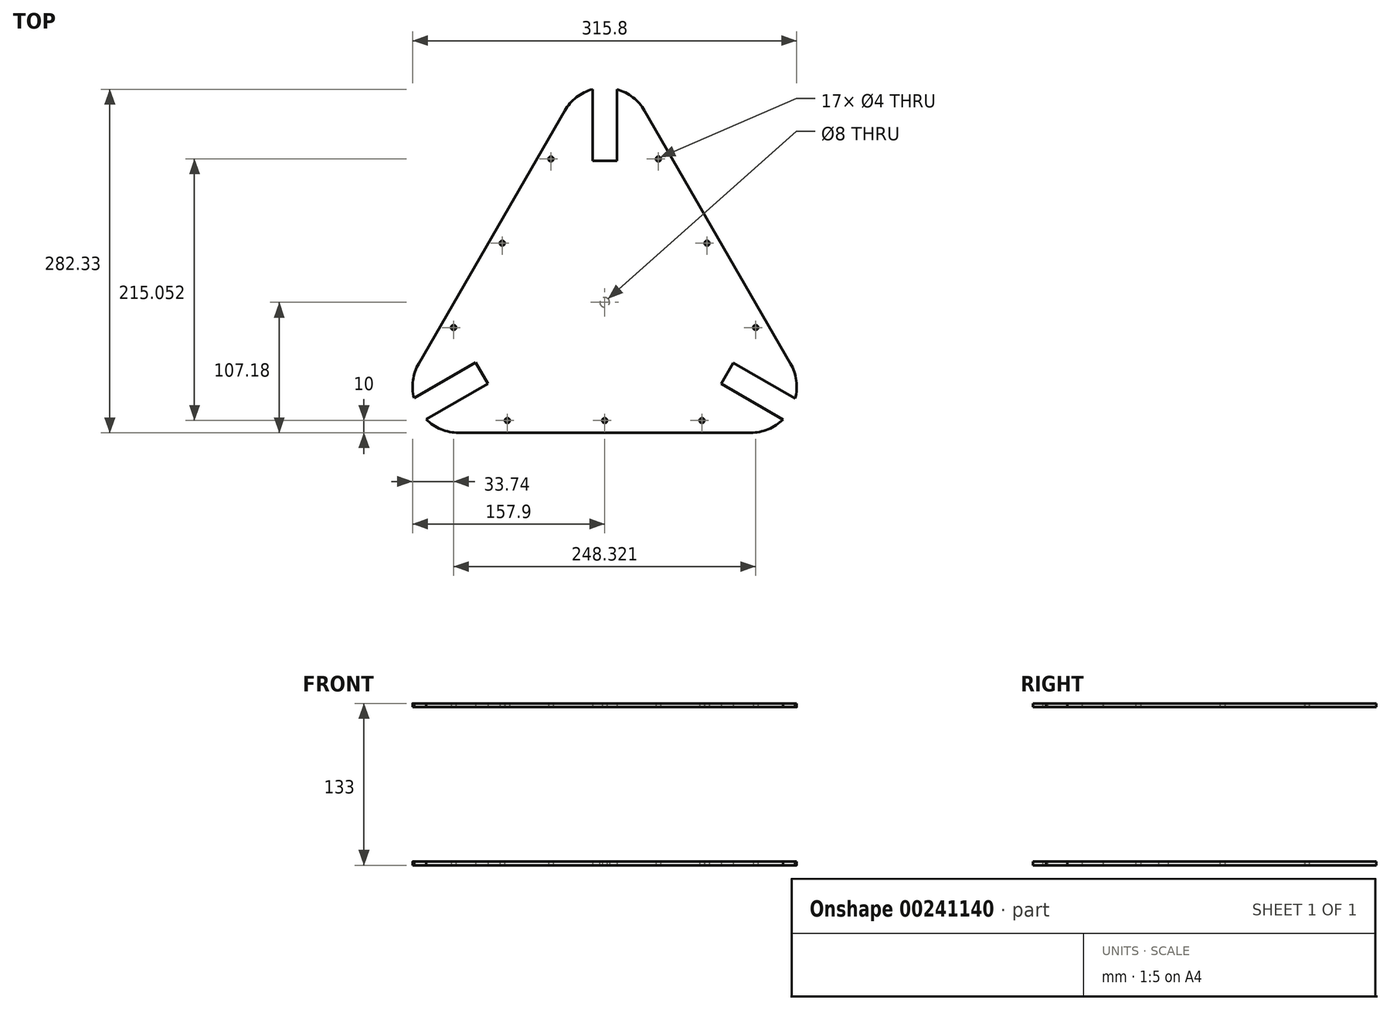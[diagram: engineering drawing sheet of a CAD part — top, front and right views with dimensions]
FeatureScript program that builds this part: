
annotation { "Feature Type Name" : "Feature", "Feature Type Description" : "" }
export const myFeature = defineFeature(function(context is Context, id is Id, definition is map)
    precondition{}
    {
        {
            var Q0;
            Q0=qCreatedBy(makeId("Top.planeOp"),FACE);
            var sketch = newSketch(context, id + "F0", { "sketchPlane" : qUnion([Q0])});
            skLineSegment(sketch, "E0.bottom", {"start": v(-120, -87.18) * mm, "end": v(120, -87.18) * mm});
            skLineSegment(sketch, "E0.top", {"start": v(-120, -107.18) * mm, "end": v(120, -107.18) * mm});
            skLineSegment(sketch, "E0.left", {"start": v(-120, -87.18) * mm, "end": v(-120, -107.18) * mm});
            skLineSegment(sketch, "E0.right", {"start": v(120, -87.18) * mm, "end": v(120, -107.18) * mm});
            skLineSegment(sketch, "E1.1.0", {"start": v(135.5, -60.33) * mm, "end": v(152.82, -50.33) * mm});
            skLineSegment(sketch, "E1.1.1", {"start": v(135.5, -60.33) * mm, "end": v(15.5, 147.51) * mm});
            skLineSegment(sketch, "E1.1.2", {"start": v(152.82, -50.33) * mm, "end": v(32.82, 157.51) * mm});
            skLineSegment(sketch, "E1.1.3", {"start": v(15.5, 147.51) * mm, "end": v(32.82, 157.51) * mm});
            skLineSegment(sketch, "E1.2.0", {"start": v(-15.5, 147.51) * mm, "end": v(-32.82, 157.51) * mm});
            skLineSegment(sketch, "E1.2.1", {"start": v(-15.5, 147.51) * mm, "end": v(-135.5, -60.33) * mm});
            skLineSegment(sketch, "E1.2.2", {"start": v(-32.82, 157.51) * mm, "end": v(-152.82, -50.33) * mm});
            skLineSegment(sketch, "E1.2.3", {"start": v(-135.5, -60.33) * mm, "end": v(-152.82, -50.33) * mm});
            skPoint(sketch, "E1.center", {"position": v(0, 0) * mm});
            skArc(sketch, "E2", {"start": v(-152.82, -50.33) * mm, "mid": v(-152.82, -88.23) * mm, "end": v(-120, -107.18) * mm});
            skArc(sketch, "E3", {"start": v(120, -107.18) * mm, "mid": v(152.82, -88.23) * mm, "end": v(152.82, -50.33) * mm});
            skArc(sketch, "E4", {"start": v(32.82, 157.51) * mm, "mid": v(0, 176.46) * mm, "end": v(-32.82, 157.51) * mm});
            skPoint(sketch, "E5.orphan", {"position": v(-92.82, 53.59) * mm});
            skPoint(sketch, "E6.middle.positionSnap0", {"position": v(0, 176.46) * mm});
            skPoint(sketch, "E6.centerSnap0", {"position": v(0, 176.46) * mm});
            skLineSegment(sketch, "E7", {"start": v(-144.16, -55.33) * mm, "end": v(-129.16, -29.35) * mm, "construction": true});
            skLineSegment(sketch, "E8", {"start": v(-120, -107.18) * mm, "end": v(-120, -113.18) * mm, "construction": true});
            skLineSegment(sketch, "E9", {"start": v(-110, -113.18) * mm, "end": v(-110, -116.18) * mm});
            skLineSegment(sketch, "E10", {"start": v(-159.07, -116.18) * mm, "end": v(-159.07, -116.18) * mm});
            skPoint(sketch, "E11.visualSharp", {"position": v(-172.46, -135.5) * mm});
            skPoint(sketch, "E12.visualSharp", {"position": v(-159.07, -118.18) * mm});
            skArc(sketch, "E13", {"start": v(-120, -87.18) * mm, "mid": v(-104.5, -60.33) * mm, "end": v(-135.5, -60.33) * mm, "construction": true});
            skLineSegment(sketch, "E14", {"start": v(-92.82, 53.59) * mm, "end": v(-75.5, 43.59) * mm, "construction": true});
            skLineSegment(sketch, "E15", {"start": v(-115.56, 26.2) * mm, "end": v(-118.16, 27.7) * mm});
            skLineSegment(sketch, "E16", {"start": v(-77.66, 91.84) * mm, "end": v(-80.26, 93.34) * mm});
            skLineSegment(sketch, "E17.anchor1", {"start": v(0, 0) * mm, "end": v(158.2, -91.34) * mm, "construction": true});
            skLineSegment(sketch, "E17.anchor2", {"start": v(0, 0) * mm, "end": v(0, 180.31) * mm, "construction": true});
            skLineSegment(sketch, "E18", {"start": v(-75.5, 43.59) * mm, "end": v(-72.38, 41.79) * mm, "construction": true});
            skCircle(sketch, "E19", {"center": v(-80, -97.18) * mm, "radius": 2 * mm});
            skLineSegment(sketch, "E20.direction1", {"start": v(-80, -97.18) * mm, "end": v(-78.5, -97.18) * mm, "construction": true});
            skLineSegment(sketch, "E21.direction1", {"start": v(-80, -97.18) * mm, "end": v(-81.5, -97.18) * mm, "construction": true});
            skLineSegment(sketch, "E22", {"start": v(0, -87.18) * mm, "end": v(0, -107.18) * mm, "construction": true});
            skLineSegment(sketch, "E23", {"start": v(-120, -87.18) * mm, "end": v(-135.5, -60.33) * mm, "construction": true});
            skCircle(sketch, "E24", {"center": v(-127.75, -73.76) * mm, "radius": 4 * mm});
            skLineSegment(sketch, "E25", {"start": v(-129.8, -50.45) * mm, "end": v(-108.59, -87.18) * mm, "construction": true});
            skLineSegment(sketch, "E26.MirrorCS", {"start": v(80, -97.18) * mm, "end": v(78.5, -97.18) * mm, "construction": true});
            skLineSegment(sketch, "E27.MirrorCS", {"start": v(80, -97.18) * mm, "end": v(81.5, -97.18) * mm, "construction": true});
            skCircle(sketch, "E28.MirrorC", {"center": v(80, -97.18) * mm, "radius": 2 * mm});
            skCircle(sketch, "E29.1.2", {"center": v(127.8, -73.86) * mm, "radius": 4 * mm});
            skCircle(sketch, "E29.2.2", {"center": v(0.12, 147.51) * mm, "radius": 4 * mm});
            skPoint(sketch, "E29.center", {"position": v(0.06, -0.03) * mm});
            skCircle(sketch, "E30", {"center": v(0, 0) * mm, "radius": 4 * mm});
            skLineSegment(sketch, "E31", {"start": v(0, 116.46) * mm, "end": v(-29.5, 116.46) * mm, "construction": true});
            skLineSegment(sketch, "E32.bottom", {"start": v(-9.88, 185.6) * mm, "end": v(10.12, 185.6) * mm});
            skLineSegment(sketch, "E32.left", {"start": v(-9.88, 185.6) * mm, "end": v(-9.88, 109.43) * mm});
            skLineSegment(sketch, "E32.right", {"start": v(10.12, 185.6) * mm, "end": v(10.12, 109.43) * mm});
            skLineSegment(sketch, "E33", {"start": v(-9.88, 116.46) * mm, "end": v(10.12, 116.46) * mm});
            skArc(sketch, "E34", {"start": v(-9.88, 104.53) * mm, "mid": v(0.12, 102.8) * mm, "end": v(10.12, 104.51) * mm});
            skLineSegment(sketch, "E35.1.0", {"start": v(-155.79, -101.35) * mm, "end": v(-89.83, -63.27) * mm});
            skLineSegment(sketch, "E35.1.1", {"start": v(-95.92, -66.79) * mm, "end": v(-105.92, -49.47) * mm});
            skLineSegment(sketch, "E35.1.2", {"start": v(-165.79, -84.03) * mm, "end": v(-99.83, -45.95) * mm});
            skLineSegment(sketch, "E35.2.0", {"start": v(165.67, -84.24) * mm, "end": v(99.71, -46.16) * mm});
            skLineSegment(sketch, "E35.2.1", {"start": v(105.8, -49.67) * mm, "end": v(95.8, -67) * mm});
            skLineSegment(sketch, "E35.2.2", {"start": v(155.67, -101.56) * mm, "end": v(89.71, -63.48) * mm});
            skCircle(sketch, "E36.1.0", {"center": v(124.16, -20.7) * mm, "radius": 2 * mm});
            skCircle(sketch, "E36.1.1", {"center": v(44.16, 117.87) * mm, "radius": 2 * mm});
            skCircle(sketch, "E36.2.0", {"center": v(-44.16, 117.87) * mm, "radius": 2 * mm});
            skCircle(sketch, "E36.2.1", {"center": v(-124.16, -20.7) * mm, "radius": 2 * mm});
            skCircle(sketch, "E37", {"center": v(0, -97.18) * mm, "radius": 2 * mm});
            skCircle(sketch, "E38.1.0", {"center": v(84.16, 48.59) * mm, "radius": 2 * mm});
            skCircle(sketch, "E38.2.0", {"center": v(-84.16, 48.59) * mm, "radius": 2 * mm});
            skSolve(sketch);
        }
        {
            var Q0;
            {var subQ0=sQuery(id+"F0.wireOp",EDGE,"E21.1.0.0");var subQ1=sQuery(id+"F0.wireOp",EDGE,"E20.2.0.0");var subQ2=makeQuery(id+"F0.imprint","INTERSECT",VERTEX,{"disambiguationData":[OD(0.0)],"derivedFrom":[subQ1,subQ0]});Q0=makeQuery(id+"F0.imprint","IMPRINT",FACE,{"disambiguationData":[TD([[makeQuery(id+"F0.imprint","IMPRINT",EDGE,{"disambiguationData":[TD([[subQ2,-1.0]])],"derivedFrom":subQ1}),1.0]])]});}
            var Q1;
            {var subQ0=sQuery(id+"F0.wireOp",EDGE,"E20.2.0.0");var subQ1=sQuery(id+"F0.wireOp",EDGE,"E20.1.0.0");var subQ2=makeQuery(id+"F0.imprint","INTERSECT",VERTEX,{"disambiguationData":[OD(0.0)],"derivedFrom":[subQ1,subQ0]});Q1=makeQuery(id+"F0.imprint","IMPRINT",FACE,{"disambiguationData":[TD([[makeQuery(id+"F0.imprint","IMPRINT",EDGE,{"disambiguationData":[TD([[subQ2,1.0]])],"derivedFrom":subQ1}),-1.0]])]});}
            var Q2;
            {var subQ0=sQuery(id+"F0.wireOp",EDGE,"E21.2.0.0");var subQ1=sQuery(id+"F0.wireOp",EDGE,"E21.1.0.0");var subQ2=makeQuery(id+"F0.imprint","INTERSECT",VERTEX,{"disambiguationData":[OD(0.0)],"derivedFrom":[subQ1,subQ0]});Q2=makeQuery(id+"F0.imprint","IMPRINT",FACE,{"disambiguationData":[TD([[makeQuery(id+"F0.imprint","IMPRINT",EDGE,{"disambiguationData":[TD([[subQ2,-1.0]])],"derivedFrom":subQ1}),-1.0]])]});}
            var Q3;
            {var subQ0=sQuery(id+"F0.wireOp",EDGE,"E21.2.0.0");var subQ1=sQuery(id+"F0.wireOp",EDGE,"E20.1.0.0");var subQ2=makeQuery(id+"F0.imprint","INTERSECT",VERTEX,{"disambiguationData":[OD(1.0)],"derivedFrom":[subQ1,subQ0]});Q3=makeQuery(id+"F0.imprint","IMPRINT",FACE,{"disambiguationData":[TD([[makeQuery(id+"F0.imprint","IMPRINT",EDGE,{"disambiguationData":[TD([[subQ2,-1.0]])],"derivedFrom":subQ1}),1.0]])]});}
            var Q4;
            {var subQ0=sQuery(id+"F0.wireOp",EDGE,"E20.2.0.0");var subQ1=sQuery(id+"F0.wireOp",EDGE,"E19");var subQ2=makeQuery(id+"F0.imprint","INTERSECT",VERTEX,{"disambiguationData":[OD(0.0)],"derivedFrom":[subQ1,subQ0]});Q4=makeQuery(id+"F0.imprint","IMPRINT",FACE,{"disambiguationData":[TD([[makeQuery(id+"F0.imprint","IMPRINT",EDGE,{"disambiguationData":[TD([[subQ2,1.0]])],"derivedFrom":subQ1}),1.0]])]});}
            var Q5;
            {var subQ0=sQuery(id+"F0.wireOp",EDGE,"E21.1.0.0");var subQ1=sQuery(id+"F0.wireOp",EDGE,"E20.1.0.0");var subQ2=makeQuery(id+"F0.imprint","INTERSECT",VERTEX,{"disambiguationData":[OD(0.0)],"derivedFrom":[subQ1,subQ0]});Q5=makeQuery(id+"F0.imprint","IMPRINT",FACE,{"disambiguationData":[TD([[makeQuery(id+"F0.imprint","IMPRINT",EDGE,{"disambiguationData":[TD([[subQ2,-1.0]])],"derivedFrom":subQ1}),1.0]])]});}
            var Q6;
            {var subQ0=sQuery(id+"F0.wireOp",EDGE,"E21.2.0.0");var subQ1=sQuery(id+"F0.wireOp",EDGE,"E19");var subQ2=makeQuery(id+"F0.imprint","INTERSECT",VERTEX,{"disambiguationData":[OD(0.0)],"derivedFrom":[subQ1,subQ0]});Q6=makeQuery(id+"F0.imprint","IMPRINT",FACE,{"disambiguationData":[TD([[makeQuery(id+"F0.imprint","IMPRINT",EDGE,{"disambiguationData":[TD([[subQ2,-1.0]])],"derivedFrom":subQ1}),1.0]])]});}
            var Q7;
            {var subQ0=sQuery(id+"F0.wireOp",EDGE,"E21.2.0.0");var subQ1=sQuery(id+"F0.wireOp",EDGE,"E19");var subQ2=makeQuery(id+"F0.imprint","INTERSECT",VERTEX,{"disambiguationData":[OD(0.0)],"derivedFrom":[subQ1,subQ0]});Q7=makeQuery(id+"F0.imprint","IMPRINT",FACE,{"disambiguationData":[TD([[makeQuery(id+"F0.imprint","IMPRINT",EDGE,{"disambiguationData":[TD([[subQ2,-1.0]])],"derivedFrom":subQ1}),-1.0]])]});}
            var Q8;
            {var subQ0=sQuery(id+"F0.wireOp",EDGE,"E20.2.0.0");var subQ1=sQuery(id+"F0.wireOp",EDGE,"E19");var subQ2=makeQuery(id+"F0.imprint","INTERSECT",VERTEX,{"disambiguationData":[OD(0.0)],"derivedFrom":[subQ1,subQ0]});Q8=makeQuery(id+"F0.imprint","IMPRINT",FACE,{"disambiguationData":[TD([[makeQuery(id+"F0.imprint","IMPRINT",EDGE,{"disambiguationData":[TD([[subQ2,1.0]])],"derivedFrom":subQ1}),-1.0]])]});}
            var Q9;
            {var subQ0=sQuery(id+"F0.wireOp",EDGE,"E20.1.0.0");var subQ1=sQuery(id+"F0.wireOp",EDGE,"E19");var subQ2=makeQuery(id+"F0.imprint","INTERSECT",VERTEX,{"disambiguationData":[OD(0.0)],"derivedFrom":[subQ1,subQ0]});Q9=makeQuery(id+"F0.imprint","IMPRINT",FACE,{"disambiguationData":[TD([[makeQuery(id+"F0.imprint","IMPRINT",EDGE,{"disambiguationData":[TD([[subQ2,1.0]])],"derivedFrom":subQ1}),1.0]])]});}
            var Q10;
            {var subQ0=sQuery(id+"F0.wireOp",EDGE,"E20.1.0.0");var subQ1=sQuery(id+"F0.wireOp",EDGE,"E19");var subQ2=makeQuery(id+"F0.imprint","INTERSECT",VERTEX,{"disambiguationData":[OD(0.0)],"derivedFrom":[subQ1,subQ0]});Q10=makeQuery(id+"F0.imprint","IMPRINT",FACE,{"disambiguationData":[TD([[makeQuery(id+"F0.imprint","IMPRINT",EDGE,{"disambiguationData":[TD([[subQ2,-1.0]])],"derivedFrom":subQ1}),1.0]])]});}
            var Q11;
            {var subQ0=sQuery(id+"F0.wireOp",EDGE,"E21.1.0.0");var subQ1=sQuery(id+"F0.wireOp",EDGE,"E19");var subQ2=makeQuery(id+"F0.imprint","INTERSECT",VERTEX,{"disambiguationData":[OD(0.0)],"derivedFrom":[subQ1,subQ0]});Q11=makeQuery(id+"F0.imprint","IMPRINT",FACE,{"disambiguationData":[TD([[makeQuery(id+"F0.imprint","IMPRINT",EDGE,{"disambiguationData":[TD([[subQ2,-1.0]])],"derivedFrom":subQ1}),-1.0]])]});}
            var Q12;
            {var subQ0=sQuery(id+"F0.wireOp",EDGE,"E21.2.0.0");var subQ1=sQuery(id+"F0.wireOp",EDGE,"E20.1.0.0");var subQ2=makeQuery(id+"F0.imprint","INTERSECT",VERTEX,{"disambiguationData":[OD(0.0)],"derivedFrom":[subQ1,subQ0]});Q12=makeQuery(id+"F0.imprint","IMPRINT",FACE,{"disambiguationData":[TD([[makeQuery(id+"F0.imprint","IMPRINT",EDGE,{"disambiguationData":[TD([[subQ2,-1.0]])],"derivedFrom":subQ1}),1.0]])]});}
            var Q13;
            {var subQ0=sQuery(id+"F0.wireOp",EDGE,"E21.1.0.0");var subQ1=sQuery(id+"F0.wireOp",EDGE,"E19");var subQ2=makeQuery(id+"F0.imprint","INTERSECT",VERTEX,{"disambiguationData":[OD(1.0)],"derivedFrom":[subQ1,subQ0]});Q13=makeQuery(id+"F0.imprint","IMPRINT",FACE,{"disambiguationData":[TD([[makeQuery(id+"F0.imprint","IMPRINT",EDGE,{"disambiguationData":[TD([[subQ2,-1.0]])],"derivedFrom":subQ1}),1.0]])]});}
            var Q14;
            {var subQ0=sQuery(id+"F0.wireOp",EDGE,"E20.1.0.0");var subQ1=sQuery(id+"F0.wireOp",EDGE,"E19");var subQ2=makeQuery(id+"F0.imprint","INTERSECT",VERTEX,{"disambiguationData":[OD(1.0)],"derivedFrom":[subQ1,subQ0]});Q14=makeQuery(id+"F0.imprint","IMPRINT",FACE,{"disambiguationData":[TD([[makeQuery(id+"F0.imprint","IMPRINT",EDGE,{"disambiguationData":[TD([[subQ2,-1.0]])],"derivedFrom":subQ1}),-1.0]])]});}
            var Q15;
            {var subQ0=sQuery(id+"F0.wireOp",EDGE,"E20.1.0.0");var subQ1=sQuery(id+"F0.wireOp",EDGE,"E19");var subQ2=makeQuery(id+"F0.imprint","INTERSECT",VERTEX,{"disambiguationData":[OD(0.0)],"derivedFrom":[subQ1,subQ0]});Q15=makeQuery(id+"F0.imprint","IMPRINT",FACE,{"disambiguationData":[TD([[makeQuery(id+"F0.imprint","IMPRINT",EDGE,{"disambiguationData":[TD([[subQ2,1.0]])],"derivedFrom":subQ1}),-1.0]])]});}
            var Q16;
            {var subQ0=sQuery(id+"F0.wireOp",EDGE,"E21.1.0.0");var subQ1=sQuery(id+"F0.wireOp",EDGE,"E19");var subQ2=makeQuery(id+"F0.imprint","INTERSECT",VERTEX,{"disambiguationData":[OD(0.0)],"derivedFrom":[subQ1,subQ0]});Q16=makeQuery(id+"F0.imprint","IMPRINT",FACE,{"disambiguationData":[TD([[makeQuery(id+"F0.imprint","IMPRINT",EDGE,{"disambiguationData":[TD([[subQ2,-1.0]])],"derivedFrom":subQ1}),1.0]])]});}
            var Q17;
            {var subQ0=sQuery(id+"F0.wireOp",EDGE,"E21.2.0.0");var subQ1=sQuery(id+"F0.wireOp",EDGE,"E19");var subQ2=makeQuery(id+"F0.imprint","INTERSECT",VERTEX,{"disambiguationData":[OD(1.0)],"derivedFrom":[subQ1,subQ0]});Q17=makeQuery(id+"F0.imprint","IMPRINT",FACE,{"disambiguationData":[TD([[makeQuery(id+"F0.imprint","IMPRINT",EDGE,{"disambiguationData":[TD([[subQ2,-1.0]])],"derivedFrom":subQ1}),1.0]])]});}
            var Q18;
            {var subQ0=sQuery(id+"F0.wireOp",EDGE,"E21.2.0.0");var subQ1=sQuery(id+"F0.wireOp",EDGE,"E19");var subQ2=makeQuery(id+"F0.imprint","INTERSECT",VERTEX,{"disambiguationData":[OD(1.0)],"derivedFrom":[subQ1,subQ0]});Q18=makeQuery(id+"F0.imprint","IMPRINT",FACE,{"disambiguationData":[TD([[makeQuery(id+"F0.imprint","IMPRINT",EDGE,{"disambiguationData":[TD([[subQ2,-1.0]])],"derivedFrom":subQ1}),-1.0]])]});}
            var Q19;
            {var subQ0=sQuery(id+"F0.wireOp",EDGE,"E20.1.0.0");var subQ1=sQuery(id+"F0.wireOp",EDGE,"E19");var subQ2=makeQuery(id+"F0.imprint","INTERSECT",VERTEX,{"disambiguationData":[OD(1.0)],"derivedFrom":[subQ1,subQ0]});Q19=makeQuery(id+"F0.imprint","IMPRINT",FACE,{"disambiguationData":[TD([[makeQuery(id+"F0.imprint","IMPRINT",EDGE,{"disambiguationData":[TD([[subQ2,-1.0]])],"derivedFrom":subQ1}),1.0]])]});}
            var Q20;
            {var subQ0=sQuery(id+"F0.wireOp",EDGE,"df970ebe-b7b2-4de3-9d96-1b594ea6aba34.MirrorC");var subQ1=sQuery(id+"F0.wireOp",EDGE,"df970ebe-b7b2-4de3-9d96-1b594ea6aba33.MirrorC");var subQ2=makeQuery(id+"F0.imprint","INTERSECT",VERTEX,{"disambiguationData":[OD(0.0)],"derivedFrom":[subQ1,subQ0]});Q20=makeQuery(id+"F0.imprint","IMPRINT",FACE,{"disambiguationData":[TD([[makeQuery(id+"F0.imprint","IMPRINT",EDGE,{"disambiguationData":[TD([[subQ2,-1.0]])],"derivedFrom":subQ1}),-1.0]])]});}
            var Q21;
            {var subQ0=sQuery(id+"F0.wireOp",EDGE,"df970ebe-b7b2-4de3-9d96-1b594ea6aba36.MirrorC");var subQ1=sQuery(id+"F0.wireOp",EDGE,"df970ebe-b7b2-4de3-9d96-1b594ea6aba32.MirrorC");var subQ2=makeQuery(id+"F0.imprint","INTERSECT",VERTEX,{"disambiguationData":[OD(0.0)],"derivedFrom":[subQ1,subQ0]});Q21=makeQuery(id+"F0.imprint","IMPRINT",FACE,{"disambiguationData":[TD([[makeQuery(id+"F0.imprint","IMPRINT",EDGE,{"disambiguationData":[TD([[subQ2,-1.0]])],"derivedFrom":subQ1}),1.0]])]});}
            var Q22;
            {var subQ0=sQuery(id+"F0.wireOp",EDGE,"E28.MirrorC");var subQ1=sQuery(id+"F0.wireOp",EDGE,"df970ebe-b7b2-4de3-9d96-1b594ea6aba32.MirrorC");var subQ2=makeQuery(id+"F0.imprint","INTERSECT",VERTEX,{"disambiguationData":[OD(0.0)],"derivedFrom":[subQ1,subQ0]});Q22=makeQuery(id+"F0.imprint","IMPRINT",FACE,{"disambiguationData":[TD([[makeQuery(id+"F0.imprint","IMPRINT",EDGE,{"disambiguationData":[TD([[subQ2,1.0]])],"derivedFrom":subQ1}),-1.0]])]});}
            var Q23;
            {var subQ0=sQuery(id+"F0.wireOp",EDGE,"E28.MirrorC");var subQ1=sQuery(id+"F0.wireOp",EDGE,"df970ebe-b7b2-4de3-9d96-1b594ea6aba33.MirrorC");var subQ2=makeQuery(id+"F0.imprint","INTERSECT",VERTEX,{"disambiguationData":[OD(0.0)],"derivedFrom":[subQ1,subQ0]});Q23=makeQuery(id+"F0.imprint","IMPRINT",FACE,{"disambiguationData":[TD([[makeQuery(id+"F0.imprint","IMPRINT",EDGE,{"disambiguationData":[TD([[subQ2,-1.0]])],"derivedFrom":subQ1}),-1.0]])]});}
            var Q24;
            {var subQ0=sQuery(id+"F0.wireOp",EDGE,"df970ebe-b7b2-4de3-9d96-1b594ea6aba36.MirrorC");var subQ1=sQuery(id+"F0.wireOp",EDGE,"df970ebe-b7b2-4de3-9d96-1b594ea6aba32.MirrorC");var subQ2=makeQuery(id+"F0.imprint","INTERSECT",VERTEX,{"disambiguationData":[OD(0.0)],"derivedFrom":[subQ1,subQ0]});Q24=makeQuery(id+"F0.imprint","IMPRINT",FACE,{"disambiguationData":[TD([[makeQuery(id+"F0.imprint","IMPRINT",EDGE,{"disambiguationData":[TD([[subQ2,-1.0]])],"derivedFrom":subQ1}),-1.0]])]});}
            var Q25;
            {var subQ0=sQuery(id+"F0.wireOp",EDGE,"E28.MirrorC");var subQ1=sQuery(id+"F0.wireOp",EDGE,"df970ebe-b7b2-4de3-9d96-1b594ea6aba32.MirrorC");var subQ2=makeQuery(id+"F0.imprint","INTERSECT",VERTEX,{"disambiguationData":[OD(0.0)],"derivedFrom":[subQ1,subQ0]});Q25=makeQuery(id+"F0.imprint","IMPRINT",FACE,{"disambiguationData":[TD([[makeQuery(id+"F0.imprint","IMPRINT",EDGE,{"disambiguationData":[TD([[subQ2,-1.0]])],"derivedFrom":subQ1}),-1.0]])]});}
            var Q26;
            {var subQ0=sQuery(id+"F0.wireOp",EDGE,"df970ebe-b7b2-4de3-9d96-1b594ea6aba34.MirrorC");var subQ1=sQuery(id+"F0.wireOp",EDGE,"df970ebe-b7b2-4de3-9d96-1b594ea6aba32.MirrorC");var subQ2=makeQuery(id+"F0.imprint","INTERSECT",VERTEX,{"disambiguationData":[OD(0.0)],"derivedFrom":[subQ1,subQ0]});Q26=makeQuery(id+"F0.imprint","IMPRINT",FACE,{"disambiguationData":[TD([[makeQuery(id+"F0.imprint","IMPRINT",EDGE,{"disambiguationData":[TD([[subQ2,1.0]])],"derivedFrom":subQ1}),-1.0]])]});}
            var Q27;
            {var subQ0=sQuery(id+"F0.wireOp",EDGE,"df970ebe-b7b2-4de3-9d96-1b594ea6aba36.MirrorC");var subQ1=sQuery(id+"F0.wireOp",EDGE,"df970ebe-b7b2-4de3-9d96-1b594ea6aba33.MirrorC");var subQ2=makeQuery(id+"F0.imprint","INTERSECT",VERTEX,{"disambiguationData":[OD(0.0)],"derivedFrom":[subQ1,subQ0]});Q27=makeQuery(id+"F0.imprint","IMPRINT",FACE,{"disambiguationData":[TD([[makeQuery(id+"F0.imprint","IMPRINT",EDGE,{"disambiguationData":[TD([[subQ2,-1.0]])],"derivedFrom":subQ1}),-1.0]])]});}
            var Q28;
            {var subQ0=sQuery(id+"F0.wireOp",EDGE,"df970ebe-b7b2-4de3-9d96-1b594ea6aba36.MirrorC");var subQ1=sQuery(id+"F0.wireOp",EDGE,"df970ebe-b7b2-4de3-9d96-1b594ea6aba32.MirrorC");var subQ2=makeQuery(id+"F0.imprint","INTERSECT",VERTEX,{"disambiguationData":[OD(1.0)],"derivedFrom":[subQ1,subQ0]});Q28=makeQuery(id+"F0.imprint","IMPRINT",FACE,{"disambiguationData":[TD([[makeQuery(id+"F0.imprint","IMPRINT",EDGE,{"disambiguationData":[TD([[subQ2,-1.0]])],"derivedFrom":subQ1}),1.0]])]});}
            var Q29;
            {var subQ0=sQuery(id+"F0.wireOp",EDGE,"E28.MirrorC");var subQ1=sQuery(id+"F0.wireOp",EDGE,"df970ebe-b7b2-4de3-9d96-1b594ea6aba32.MirrorC");var subQ2=makeQuery(id+"F0.imprint","INTERSECT",VERTEX,{"disambiguationData":[OD(1.0)],"derivedFrom":[subQ1,subQ0]});Q29=makeQuery(id+"F0.imprint","IMPRINT",FACE,{"disambiguationData":[TD([[makeQuery(id+"F0.imprint","IMPRINT",EDGE,{"disambiguationData":[TD([[subQ2,-1.0]])],"derivedFrom":subQ1}),1.0]])]});}
            var Q30;
            {var subQ0=sQuery(id+"F0.wireOp",EDGE,"E28.MirrorC");var subQ1=sQuery(id+"F0.wireOp",EDGE,"df970ebe-b7b2-4de3-9d96-1b594ea6aba32.MirrorC");var subQ2=makeQuery(id+"F0.imprint","INTERSECT",VERTEX,{"disambiguationData":[OD(0.0)],"derivedFrom":[subQ1,subQ0]});Q30=makeQuery(id+"F0.imprint","IMPRINT",FACE,{"disambiguationData":[TD([[makeQuery(id+"F0.imprint","IMPRINT",EDGE,{"disambiguationData":[TD([[subQ2,1.0]])],"derivedFrom":subQ1}),1.0]])]});}
            var Q31;
            {var subQ0=sQuery(id+"F0.wireOp",EDGE,"df970ebe-b7b2-4de3-9d96-1b594ea6aba33.MirrorC");var subQ1=sQuery(id+"F0.wireOp",EDGE,"df970ebe-b7b2-4de3-9d96-1b594ea6aba32.MirrorC");var subQ2=makeQuery(id+"F0.imprint","INTERSECT",VERTEX,{"derivedFrom":[subQ1,subQ0]});Q31=makeQuery(id+"F0.imprint","IMPRINT",FACE,{"disambiguationData":[TD([[makeQuery(id+"F0.imprint","IMPRINT",EDGE,{"disambiguationData":[TD([[subQ2,-1.0]])],"derivedFrom":subQ1}),1.0]])]});}
            var Q32;
            {var subQ0=sQuery(id+"F0.wireOp",EDGE,"E28.MirrorC");var subQ1=sQuery(id+"F0.wireOp",EDGE,"df970ebe-b7b2-4de3-9d96-1b594ea6aba33.MirrorC");var subQ2=makeQuery(id+"F0.imprint","INTERSECT",VERTEX,{"disambiguationData":[OD(0.0)],"derivedFrom":[subQ1,subQ0]});Q32=makeQuery(id+"F0.imprint","IMPRINT",FACE,{"disambiguationData":[TD([[makeQuery(id+"F0.imprint","IMPRINT",EDGE,{"disambiguationData":[TD([[subQ2,-1.0]])],"derivedFrom":subQ1}),1.0]])]});}
            var Q33;
            {var subQ0=sQuery(id+"F0.wireOp",EDGE,"df970ebe-b7b2-4de3-9d96-1b594ea6aba33.MirrorC");var subQ1=makeQuery(id+"F0.imprint","INTERSECT",VERTEX,{"derivedFrom":[sQuery(id+"F0.wireOp",EDGE,"df970ebe-b7b2-4de3-9d96-1b594ea6aba32.MirrorC"),subQ0]});Q33=makeQuery(id+"F0.imprint","IMPRINT",FACE,{"disambiguationData":[TD([[makeQuery(id+"F0.imprint","IMPRINT",EDGE,{"disambiguationData":[TD([[subQ1,-1.0]])],"derivedFrom":subQ0}),-1.0]])]});}
            var Q34;
            {var subQ0=sQuery(id+"F0.wireOp",EDGE,"df970ebe-b7b2-4de3-9d96-1b594ea6aba34.MirrorC");var subQ1=sQuery(id+"F0.wireOp",EDGE,"df970ebe-b7b2-4de3-9d96-1b594ea6aba33.MirrorC");var subQ2=makeQuery(id+"F0.imprint","INTERSECT",VERTEX,{"disambiguationData":[OD(0.0)],"derivedFrom":[subQ1,subQ0]});Q34=makeQuery(id+"F0.imprint","IMPRINT",FACE,{"disambiguationData":[TD([[makeQuery(id+"F0.imprint","IMPRINT",EDGE,{"disambiguationData":[TD([[subQ2,-1.0]])],"derivedFrom":subQ1}),1.0]])]});}
            var Q35;
            {var subQ0=sQuery(id+"F0.wireOp",EDGE,"df970ebe-b7b2-4de3-9d96-1b594ea6aba36.MirrorC");var subQ1=sQuery(id+"F0.wireOp",EDGE,"df970ebe-b7b2-4de3-9d96-1b594ea6aba34.MirrorC");var subQ2=makeQuery(id+"F0.imprint","INTERSECT",VERTEX,{"disambiguationData":[OD(1.0)],"derivedFrom":[subQ1,subQ0]});Q35=makeQuery(id+"F0.imprint","IMPRINT",FACE,{"disambiguationData":[TD([[makeQuery(id+"F0.imprint","IMPRINT",EDGE,{"disambiguationData":[TD([[subQ2,-1.0]])],"derivedFrom":subQ1}),1.0]])]});}
            var Q36;
            {var subQ0=sQuery(id+"F0.wireOp",EDGE,"E28.MirrorC");var subQ1=sQuery(id+"F0.wireOp",EDGE,"df970ebe-b7b2-4de3-9d96-1b594ea6aba32.MirrorC");var subQ2=makeQuery(id+"F0.imprint","INTERSECT",VERTEX,{"disambiguationData":[OD(0.0)],"derivedFrom":[subQ1,subQ0]});Q36=makeQuery(id+"F0.imprint","IMPRINT",FACE,{"disambiguationData":[TD([[makeQuery(id+"F0.imprint","IMPRINT",EDGE,{"disambiguationData":[TD([[subQ2,-1.0]])],"derivedFrom":subQ1}),1.0]])]});}
            var Q37;
            {var subQ0=sQuery(id+"F0.wireOp",EDGE,"E28.MirrorC");var subQ1=sQuery(id+"F0.wireOp",EDGE,"df970ebe-b7b2-4de3-9d96-1b594ea6aba33.MirrorC");var subQ2=makeQuery(id+"F0.imprint","INTERSECT",VERTEX,{"disambiguationData":[OD(1.0)],"derivedFrom":[subQ1,subQ0]});Q37=makeQuery(id+"F0.imprint","IMPRINT",FACE,{"disambiguationData":[TD([[makeQuery(id+"F0.imprint","IMPRINT",EDGE,{"disambiguationData":[TD([[subQ2,-1.0]])],"derivedFrom":subQ1}),1.0]])]});}
            var Q38;
            {var subQ0=sQuery(id+"F0.wireOp",EDGE,"df970ebe-b7b2-4de3-9d96-1b594ea6aba36.MirrorC");var subQ1=sQuery(id+"F0.wireOp",EDGE,"df970ebe-b7b2-4de3-9d96-1b594ea6aba33.MirrorC");var subQ2=makeQuery(id+"F0.imprint","INTERSECT",VERTEX,{"disambiguationData":[OD(1.0)],"derivedFrom":[subQ1,subQ0]});Q38=makeQuery(id+"F0.imprint","IMPRINT",FACE,{"disambiguationData":[TD([[makeQuery(id+"F0.imprint","IMPRINT",EDGE,{"disambiguationData":[TD([[subQ2,-1.0]])],"derivedFrom":subQ1}),1.0]])]});}
            var Q39;
            {var subQ0=sQuery(id+"F0.wireOp",EDGE,"E28.MirrorC");var subQ1=sQuery(id+"F0.wireOp",EDGE,"df970ebe-b7b2-4de3-9d96-1b594ea6aba34.MirrorC");var subQ2=makeQuery(id+"F0.imprint","INTERSECT",VERTEX,{"disambiguationData":[OD(0.0)],"derivedFrom":[subQ1,subQ0]});Q39=makeQuery(id+"F0.imprint","IMPRINT",FACE,{"disambiguationData":[TD([[makeQuery(id+"F0.imprint","IMPRINT",EDGE,{"disambiguationData":[TD([[subQ2,-1.0]])],"derivedFrom":subQ1}),1.0]])]});}
            var Q40;
            {var subQ0=sQuery(id+"F0.wireOp",EDGE,"E29.1.6");var subQ1=sQuery(id+"F0.wireOp",EDGE,"E29.1.4");var subQ2=makeQuery(id+"F0.imprint","INTERSECT",VERTEX,{"disambiguationData":[OD(0.0)],"derivedFrom":[subQ1,subQ0]});Q40=makeQuery(id+"F0.imprint","IMPRINT",FACE,{"disambiguationData":[TD([[makeQuery(id+"F0.imprint","IMPRINT",EDGE,{"disambiguationData":[TD([[subQ2,1.0]])],"derivedFrom":subQ1}),1.0]])]});}
            var Q41;
            {var subQ0=sQuery(id+"F0.wireOp",EDGE,"E29.1.5");var subQ1=sQuery(id+"F0.wireOp",EDGE,"E29.1.4");var subQ2=makeQuery(id+"F0.imprint","INTERSECT",VERTEX,{"disambiguationData":[OD(0.0)],"derivedFrom":[subQ1,subQ0]});Q41=makeQuery(id+"F0.imprint","IMPRINT",FACE,{"disambiguationData":[TD([[makeQuery(id+"F0.imprint","IMPRINT",EDGE,{"disambiguationData":[TD([[subQ2,1.0]])],"derivedFrom":subQ1}),1.0]])]});}
            var Q42;
            {var subQ0=sQuery(id+"F0.wireOp",EDGE,"E29.1.4");var subQ1=makeQuery(id+"F0.imprint","INTERSECT",VERTEX,{"derivedFrom":[sQuery(id+"F0.wireOp",EDGE,"E29.1.3"),subQ0]});Q42=makeQuery(id+"F0.imprint","IMPRINT",FACE,{"disambiguationData":[TD([[makeQuery(id+"F0.imprint","IMPRINT",EDGE,{"disambiguationData":[TD([[subQ1,1.0]])],"derivedFrom":subQ0}),1.0]])]});}
            var Q43;
            {var subQ0=sQuery(id+"F0.wireOp",EDGE,"E29.1.7");var subQ1=sQuery(id+"F0.wireOp",EDGE,"E29.1.3");var subQ2=makeQuery(id+"F0.imprint","INTERSECT",VERTEX,{"disambiguationData":[OD(0.0)],"derivedFrom":[subQ1,subQ0]});Q43=makeQuery(id+"F0.imprint","IMPRINT",FACE,{"disambiguationData":[TD([[makeQuery(id+"F0.imprint","IMPRINT",EDGE,{"disambiguationData":[TD([[subQ2,-1.0]])],"derivedFrom":subQ1}),1.0]])]});}
            var Q44;
            {var subQ0=sQuery(id+"F0.wireOp",EDGE,"E29.1.5");var subQ1=sQuery(id+"F0.wireOp",EDGE,"E29.1.3");var subQ2=makeQuery(id+"F0.imprint","INTERSECT",VERTEX,{"disambiguationData":[OD(0.0)],"derivedFrom":[subQ1,subQ0]});Q44=makeQuery(id+"F0.imprint","IMPRINT",FACE,{"disambiguationData":[TD([[makeQuery(id+"F0.imprint","IMPRINT",EDGE,{"disambiguationData":[TD([[subQ2,-1.0]])],"derivedFrom":subQ1}),1.0]])]});}
            var Q45;
            {var subQ0=sQuery(id+"F0.wireOp",EDGE,"E29.1.5");var subQ1=sQuery(id+"F0.wireOp",EDGE,"E29.1.4");var subQ2=makeQuery(id+"F0.imprint","INTERSECT",VERTEX,{"disambiguationData":[OD(0.0)],"derivedFrom":[subQ1,subQ0]});Q45=makeQuery(id+"F0.imprint","IMPRINT",FACE,{"disambiguationData":[TD([[makeQuery(id+"F0.imprint","IMPRINT",EDGE,{"disambiguationData":[TD([[subQ2,-1.0]])],"derivedFrom":subQ1}),1.0]])]});}
            var Q46;
            {var subQ19=sQuery(id+"F0.wireOp",EDGE,"E1.1.0");Q46=makeQuery(id+"F0.imprint","IMPRINT",FACE,{"disambiguationData":[TD([[makeQuery(id+"F0.imprint","IMPRINT",EDGE,{"derivedFrom":subQ19}),1.0]])]});}
            var Q47;
            {var subQ0=sQuery(id+"F0.wireOp",EDGE,"E29.1.6");var subQ1=sQuery(id+"F0.wireOp",EDGE,"E29.1.3");var subQ2=makeQuery(id+"F0.imprint","INTERSECT",VERTEX,{"disambiguationData":[OD(0.0)],"derivedFrom":[subQ1,subQ0]});Q47=makeQuery(id+"F0.imprint","IMPRINT",FACE,{"disambiguationData":[TD([[makeQuery(id+"F0.imprint","IMPRINT",EDGE,{"disambiguationData":[TD([[subQ2,-1.0]])],"derivedFrom":subQ1}),1.0]])]});}
            var Q48;
            {var subQ0=sQuery(id+"F0.wireOp",EDGE,"E29.1.7");var subQ1=sQuery(id+"F0.wireOp",EDGE,"E29.1.5");var subQ2=makeQuery(id+"F0.imprint","INTERSECT",VERTEX,{"disambiguationData":[OD(1.0)],"derivedFrom":[subQ1,subQ0]});Q48=makeQuery(id+"F0.imprint","IMPRINT",FACE,{"disambiguationData":[TD([[makeQuery(id+"F0.imprint","IMPRINT",EDGE,{"disambiguationData":[TD([[subQ2,-1.0]])],"derivedFrom":subQ1}),1.0]])]});}
            var Q49;
            {var subQ0=sQuery(id+"F0.wireOp",EDGE,"E29.1.5");var subQ1=sQuery(id+"F0.wireOp",EDGE,"E29.1.3");var subQ2=makeQuery(id+"F0.imprint","INTERSECT",VERTEX,{"disambiguationData":[OD(1.0)],"derivedFrom":[subQ1,subQ0]});Q49=makeQuery(id+"F0.imprint","IMPRINT",FACE,{"disambiguationData":[TD([[makeQuery(id+"F0.imprint","IMPRINT",EDGE,{"disambiguationData":[TD([[subQ2,-1.0]])],"derivedFrom":subQ1}),-1.0]])]});}
            var Q50;
            {var subQ0=sQuery(id+"F0.wireOp",EDGE,"E29.1.7");var subQ1=sQuery(id+"F0.wireOp",EDGE,"E29.1.3");var subQ2=makeQuery(id+"F0.imprint","INTERSECT",VERTEX,{"disambiguationData":[OD(1.0)],"derivedFrom":[subQ1,subQ0]});Q50=makeQuery(id+"F0.imprint","IMPRINT",FACE,{"disambiguationData":[TD([[makeQuery(id+"F0.imprint","IMPRINT",EDGE,{"disambiguationData":[TD([[subQ2,-1.0]])],"derivedFrom":subQ1}),-1.0]])]});}
            var Q51;
            {var subQ0=sQuery(id+"F0.wireOp",EDGE,"E29.1.6");var subQ1=sQuery(id+"F0.wireOp",EDGE,"E29.1.5");var subQ2=makeQuery(id+"F0.imprint","INTERSECT",VERTEX,{"disambiguationData":[OD(0.0)],"derivedFrom":[subQ1,subQ0]});Q51=makeQuery(id+"F0.imprint","IMPRINT",FACE,{"disambiguationData":[TD([[makeQuery(id+"F0.imprint","IMPRINT",EDGE,{"disambiguationData":[TD([[subQ2,-1.0]])],"derivedFrom":subQ1}),1.0]])]});}
            var Q52;
            {var subQ0=sQuery(id+"F0.wireOp",EDGE,"E29.1.6");var subQ1=sQuery(id+"F0.wireOp",EDGE,"E29.1.3");var subQ2=makeQuery(id+"F0.imprint","INTERSECT",VERTEX,{"disambiguationData":[OD(0.0)],"derivedFrom":[subQ1,subQ0]});Q52=makeQuery(id+"F0.imprint","IMPRINT",FACE,{"disambiguationData":[TD([[makeQuery(id+"F0.imprint","IMPRINT",EDGE,{"disambiguationData":[TD([[subQ2,1.0]])],"derivedFrom":subQ1}),1.0]])]});}
            var Q53;
            {var subQ0=sQuery(id+"F0.wireOp",EDGE,"E29.1.5");var subQ1=sQuery(id+"F0.wireOp",EDGE,"E29.1.4");var subQ2=makeQuery(id+"F0.imprint","INTERSECT",VERTEX,{"disambiguationData":[OD(1.0)],"derivedFrom":[subQ1,subQ0]});Q53=makeQuery(id+"F0.imprint","IMPRINT",FACE,{"disambiguationData":[TD([[makeQuery(id+"F0.imprint","IMPRINT",EDGE,{"disambiguationData":[TD([[subQ2,-1.0]])],"derivedFrom":subQ1}),-1.0]])]});}
            var Q54;
            {var subQ0=sQuery(id+"F0.wireOp",EDGE,"E29.1.5");var subQ1=sQuery(id+"F0.wireOp",EDGE,"E29.1.3");var subQ2=makeQuery(id+"F0.imprint","INTERSECT",VERTEX,{"disambiguationData":[OD(0.0)],"derivedFrom":[subQ1,subQ0]});Q54=makeQuery(id+"F0.imprint","IMPRINT",FACE,{"disambiguationData":[TD([[makeQuery(id+"F0.imprint","IMPRINT",EDGE,{"disambiguationData":[TD([[subQ2,-1.0]])],"derivedFrom":subQ1}),-1.0]])]});}
            var Q55;
            {var subQ0=sQuery(id+"F0.wireOp",EDGE,"E29.1.5");var subQ1=sQuery(id+"F0.wireOp",EDGE,"E29.1.4");var subQ2=makeQuery(id+"F0.imprint","INTERSECT",VERTEX,{"disambiguationData":[OD(0.0)],"derivedFrom":[subQ1,subQ0]});Q55=makeQuery(id+"F0.imprint","IMPRINT",FACE,{"disambiguationData":[TD([[makeQuery(id+"F0.imprint","IMPRINT",EDGE,{"disambiguationData":[TD([[subQ2,-1.0]])],"derivedFrom":subQ1}),-1.0]])]});}
            var Q56;
            {var subQ0=sQuery(id+"F0.wireOp",EDGE,"E29.1.7");var subQ1=sQuery(id+"F0.wireOp",EDGE,"E29.1.4");var subQ2=makeQuery(id+"F0.imprint","INTERSECT",VERTEX,{"disambiguationData":[OD(1.0)],"derivedFrom":[subQ1,subQ0]});Q56=makeQuery(id+"F0.imprint","IMPRINT",FACE,{"disambiguationData":[TD([[makeQuery(id+"F0.imprint","IMPRINT",EDGE,{"disambiguationData":[TD([[subQ2,-1.0]])],"derivedFrom":subQ1}),-1.0]])]});}
            var Q57;
            {var subQ0=sQuery(id+"F0.wireOp",EDGE,"E29.1.6");var subQ1=sQuery(id+"F0.wireOp",EDGE,"E29.1.3");var subQ2=makeQuery(id+"F0.imprint","INTERSECT",VERTEX,{"disambiguationData":[OD(0.0)],"derivedFrom":[subQ1,subQ0]});Q57=makeQuery(id+"F0.imprint","IMPRINT",FACE,{"disambiguationData":[TD([[makeQuery(id+"F0.imprint","IMPRINT",EDGE,{"disambiguationData":[TD([[subQ2,1.0]])],"derivedFrom":subQ1}),-1.0]])]});}
            var Q58;
            {var subQ0=sQuery(id+"F0.wireOp",EDGE,"E29.1.6");var subQ1=sQuery(id+"F0.wireOp",EDGE,"E29.1.3");var subQ2=makeQuery(id+"F0.imprint","INTERSECT",VERTEX,{"disambiguationData":[OD(0.0)],"derivedFrom":[subQ1,subQ0]});Q58=makeQuery(id+"F0.imprint","IMPRINT",FACE,{"disambiguationData":[TD([[makeQuery(id+"F0.imprint","IMPRINT",EDGE,{"disambiguationData":[TD([[subQ2,-1.0]])],"derivedFrom":subQ1}),-1.0]])]});}
            var Q59;
            {var subQ0=sQuery(id+"F0.wireOp",EDGE,"E29.1.5");var subQ1=sQuery(id+"F0.wireOp",EDGE,"E29.1.4");var subQ2=makeQuery(id+"F0.imprint","INTERSECT",VERTEX,{"disambiguationData":[OD(0.0)],"derivedFrom":[subQ1,subQ0]});Q59=makeQuery(id+"F0.imprint","IMPRINT",FACE,{"disambiguationData":[TD([[makeQuery(id+"F0.imprint","IMPRINT",EDGE,{"disambiguationData":[TD([[subQ2,1.0]])],"derivedFrom":subQ1}),-1.0]])]});}
            var Q60;
            {var subQ0=sQuery(id+"F0.wireOp",EDGE,"E29.1.4");var subQ1=sQuery(id+"F0.wireOp",EDGE,"E29.1.3");var subQ2=makeQuery(id+"F0.imprint","INTERSECT",VERTEX,{"derivedFrom":[subQ1,subQ0]});Q60=makeQuery(id+"F0.imprint","IMPRINT",FACE,{"disambiguationData":[TD([[makeQuery(id+"F0.imprint","IMPRINT",EDGE,{"disambiguationData":[TD([[subQ2,1.0]])],"derivedFrom":subQ1}),-1.0]])]});}
            var Q61;
            {var subQ0=sQuery(id+"F0.wireOp",EDGE,"E29.2.0");var subQ1=sQuery(id+"F0.wireOp",EDGE,"E1.1.2");var subQ2=makeQuery(id+"F0.imprint","INTERSECT",VERTEX,{"disambiguationData":[OD(0.0)],"derivedFrom":[subQ1,subQ0]});Q61=makeQuery(id+"F0.imprint","IMPRINT",FACE,{"disambiguationData":[TD([[makeQuery(id+"F0.imprint","IMPRINT",EDGE,{"disambiguationData":[TD([[subQ2,-1.0]])],"derivedFrom":subQ1}),1.0]])]});}
            var Q62;
            {var subQ0=sQuery(id+"F0.wireOp",EDGE,"E29.1.12");var subQ1=sQuery(id+"F0.wireOp",EDGE,"E29.1.10");var subQ2=makeQuery(id+"F0.imprint","INTERSECT",VERTEX,{"disambiguationData":[OD(0.0)],"derivedFrom":[subQ1,subQ0]});Q62=makeQuery(id+"F0.imprint","IMPRINT",FACE,{"disambiguationData":[TD([[makeQuery(id+"F0.imprint","IMPRINT",EDGE,{"disambiguationData":[TD([[subQ2,-1.0]])],"derivedFrom":subQ1}),-1.0]])]});}
            var Q63;
            {var subQ0=sQuery(id+"F0.wireOp",EDGE,"E29.1.12");var subQ1=sQuery(id+"F0.wireOp",EDGE,"E29.1.10");var subQ2=makeQuery(id+"F0.imprint","INTERSECT",VERTEX,{"disambiguationData":[OD(0.0)],"derivedFrom":[subQ1,subQ0]});Q63=makeQuery(id+"F0.imprint","IMPRINT",FACE,{"disambiguationData":[TD([[makeQuery(id+"F0.imprint","IMPRINT",EDGE,{"disambiguationData":[TD([[subQ2,1.0]])],"derivedFrom":subQ1}),-1.0]])]});}
            var Q64;
            {var subQ0=sQuery(id+"F0.wireOp",EDGE,"E29.1.13");var subQ1=sQuery(id+"F0.wireOp",EDGE,"E29.1.10");var subQ2=makeQuery(id+"F0.imprint","INTERSECT",VERTEX,{"disambiguationData":[OD(0.0)],"derivedFrom":[subQ1,subQ0]});Q64=makeQuery(id+"F0.imprint","IMPRINT",FACE,{"disambiguationData":[TD([[makeQuery(id+"F0.imprint","IMPRINT",EDGE,{"disambiguationData":[TD([[subQ2,1.0]])],"derivedFrom":subQ1}),-1.0]])]});}
            var Q65;
            {var subQ0=sQuery(id+"F0.wireOp",EDGE,"E29.1.12");var subQ1=sQuery(id+"F0.wireOp",EDGE,"E29.1.11");var subQ2=makeQuery(id+"F0.imprint","INTERSECT",VERTEX,{"disambiguationData":[OD(0.0)],"derivedFrom":[subQ1,subQ0]});Q65=makeQuery(id+"F0.imprint","IMPRINT",FACE,{"disambiguationData":[TD([[makeQuery(id+"F0.imprint","IMPRINT",EDGE,{"disambiguationData":[TD([[subQ2,-1.0]])],"derivedFrom":subQ1}),-1.0]])]});}
            var Q66;
            {var subQ0=sQuery(id+"F0.wireOp",EDGE,"E29.1.14");var subQ1=sQuery(id+"F0.wireOp",EDGE,"E29.1.11");var subQ2=makeQuery(id+"F0.imprint","INTERSECT",VERTEX,{"disambiguationData":[OD(0.0)],"derivedFrom":[subQ1,subQ0]});Q66=makeQuery(id+"F0.imprint","IMPRINT",FACE,{"disambiguationData":[TD([[makeQuery(id+"F0.imprint","IMPRINT",EDGE,{"disambiguationData":[TD([[subQ2,-1.0]])],"derivedFrom":subQ1}),-1.0]])]});}
            var Q67;
            {var subQ7=sQuery(id+"F0.wireOp",EDGE,"E1.1.3");Q67=makeQuery(id+"F0.imprint","IMPRINT",FACE,{"disambiguationData":[TD([[makeQuery(id+"F0.imprint","IMPRINT",EDGE,{"derivedFrom":subQ7}),-1.0]])]});}
            var Q68;
            {var subQ0=sQuery(id+"F0.wireOp",EDGE,"E29.1.13");var subQ1=sQuery(id+"F0.wireOp",EDGE,"E29.1.11");var subQ2=makeQuery(id+"F0.imprint","INTERSECT",VERTEX,{"disambiguationData":[OD(0.0)],"derivedFrom":[subQ1,subQ0]});Q68=makeQuery(id+"F0.imprint","IMPRINT",FACE,{"disambiguationData":[TD([[makeQuery(id+"F0.imprint","IMPRINT",EDGE,{"disambiguationData":[TD([[subQ2,-1.0]])],"derivedFrom":subQ1}),-1.0]])]});}
            var Q69;
            {var subQ0=sQuery(id+"F0.wireOp",EDGE,"E29.1.11");var subQ1=sQuery(id+"F0.wireOp",EDGE,"E29.1.10");var subQ2=makeQuery(id+"F0.imprint","INTERSECT",VERTEX,{"derivedFrom":[subQ1,subQ0]});Q69=makeQuery(id+"F0.imprint","IMPRINT",FACE,{"disambiguationData":[TD([[makeQuery(id+"F0.imprint","IMPRINT",EDGE,{"disambiguationData":[TD([[subQ2,-1.0]])],"derivedFrom":subQ1}),1.0]])]});}
            var Q70;
            {var subQ0=sQuery(id+"F0.wireOp",EDGE,"E29.1.12");var subQ1=sQuery(id+"F0.wireOp",EDGE,"E29.1.10");var subQ2=makeQuery(id+"F0.imprint","INTERSECT",VERTEX,{"disambiguationData":[OD(0.0)],"derivedFrom":[subQ1,subQ0]});Q70=makeQuery(id+"F0.imprint","IMPRINT",FACE,{"disambiguationData":[TD([[makeQuery(id+"F0.imprint","IMPRINT",EDGE,{"disambiguationData":[TD([[subQ2,1.0]])],"derivedFrom":subQ1}),1.0]])]});}
            var Q71;
            {var subQ0=sQuery(id+"F0.wireOp",EDGE,"E29.1.14");var subQ1=sQuery(id+"F0.wireOp",EDGE,"E29.1.10");var subQ2=makeQuery(id+"F0.imprint","INTERSECT",VERTEX,{"disambiguationData":[OD(0.0)],"derivedFrom":[subQ1,subQ0]});Q71=makeQuery(id+"F0.imprint","IMPRINT",FACE,{"disambiguationData":[TD([[makeQuery(id+"F0.imprint","IMPRINT",EDGE,{"disambiguationData":[TD([[subQ2,-1.0]])],"derivedFrom":subQ1}),1.0]])]});}
            var Q72;
            {var subQ0=sQuery(id+"F0.wireOp",EDGE,"E29.1.13");var subQ1=sQuery(id+"F0.wireOp",EDGE,"E29.1.12");var subQ2=makeQuery(id+"F0.imprint","INTERSECT",VERTEX,{"disambiguationData":[OD(0.0)],"derivedFrom":[subQ1,subQ0]});Q72=makeQuery(id+"F0.imprint","IMPRINT",FACE,{"disambiguationData":[TD([[makeQuery(id+"F0.imprint","IMPRINT",EDGE,{"disambiguationData":[TD([[subQ2,-1.0]])],"derivedFrom":subQ1}),-1.0]])]});}
            var Q73;
            {var subQ0=sQuery(id+"F0.wireOp",EDGE,"E29.1.12");var subQ1=sQuery(id+"F0.wireOp",EDGE,"E29.1.10");var subQ2=makeQuery(id+"F0.imprint","INTERSECT",VERTEX,{"disambiguationData":[OD(0.0)],"derivedFrom":[subQ1,subQ0]});Q73=makeQuery(id+"F0.imprint","IMPRINT",FACE,{"disambiguationData":[TD([[makeQuery(id+"F0.imprint","IMPRINT",EDGE,{"disambiguationData":[TD([[subQ2,-1.0]])],"derivedFrom":subQ1}),1.0]])]});}
            var Q74;
            {var subQ0=sQuery(id+"F0.wireOp",EDGE,"E29.1.14");var subQ1=sQuery(id+"F0.wireOp",EDGE,"E29.1.10");var subQ2=makeQuery(id+"F0.imprint","INTERSECT",VERTEX,{"disambiguationData":[OD(0.0)],"derivedFrom":[subQ1,subQ0]});Q74=makeQuery(id+"F0.imprint","IMPRINT",FACE,{"disambiguationData":[TD([[makeQuery(id+"F0.imprint","IMPRINT",EDGE,{"disambiguationData":[TD([[subQ2,-1.0]])],"derivedFrom":subQ1}),-1.0]])]});}
            var Q75;
            {var subQ0=sQuery(id+"F0.wireOp",EDGE,"E29.1.12");var subQ1=sQuery(id+"F0.wireOp",EDGE,"E29.1.11");var subQ2=makeQuery(id+"F0.imprint","INTERSECT",VERTEX,{"disambiguationData":[OD(0.0)],"derivedFrom":[subQ1,subQ0]});Q75=makeQuery(id+"F0.imprint","IMPRINT",FACE,{"disambiguationData":[TD([[makeQuery(id+"F0.imprint","IMPRINT",EDGE,{"disambiguationData":[TD([[subQ2,-1.0]])],"derivedFrom":subQ1}),1.0]])]});}
            var Q76;
            {var subQ0=sQuery(id+"F0.wireOp",EDGE,"E29.1.12");var subQ1=sQuery(id+"F0.wireOp",EDGE,"E29.1.10");var subQ2=makeQuery(id+"F0.imprint","INTERSECT",VERTEX,{"disambiguationData":[OD(1.0)],"derivedFrom":[subQ1,subQ0]});Q76=makeQuery(id+"F0.imprint","IMPRINT",FACE,{"disambiguationData":[TD([[makeQuery(id+"F0.imprint","IMPRINT",EDGE,{"disambiguationData":[TD([[subQ2,-1.0]])],"derivedFrom":subQ1}),1.0]])]});}
            var Q77;
            {var subQ0=sQuery(id+"F0.wireOp",EDGE,"E29.1.14");var subQ1=sQuery(id+"F0.wireOp",EDGE,"E29.1.12");var subQ2=makeQuery(id+"F0.imprint","INTERSECT",VERTEX,{"disambiguationData":[OD(1.0)],"derivedFrom":[subQ1,subQ0]});Q77=makeQuery(id+"F0.imprint","IMPRINT",FACE,{"disambiguationData":[TD([[makeQuery(id+"F0.imprint","IMPRINT",EDGE,{"disambiguationData":[TD([[subQ2,-1.0]])],"derivedFrom":subQ1}),-1.0]])]});}
            var Q78;
            {var subQ0=sQuery(id+"F0.wireOp",EDGE,"E29.1.13");var subQ1=sQuery(id+"F0.wireOp",EDGE,"E29.1.11");var subQ2=makeQuery(id+"F0.imprint","INTERSECT",VERTEX,{"disambiguationData":[OD(0.0)],"derivedFrom":[subQ1,subQ0]});Q78=makeQuery(id+"F0.imprint","IMPRINT",FACE,{"disambiguationData":[TD([[makeQuery(id+"F0.imprint","IMPRINT",EDGE,{"disambiguationData":[TD([[subQ2,-1.0]])],"derivedFrom":subQ1}),1.0]])]});}
            var Q79;
            {var subQ0=sQuery(id+"F0.wireOp",EDGE,"E29.1.11");var subQ1=makeQuery(id+"F0.imprint","INTERSECT",VERTEX,{"derivedFrom":[sQuery(id+"F0.wireOp",EDGE,"E29.1.10"),subQ0]});Q79=makeQuery(id+"F0.imprint","IMPRINT",FACE,{"disambiguationData":[TD([[makeQuery(id+"F0.imprint","IMPRINT",EDGE,{"disambiguationData":[TD([[subQ1,-1.0]])],"derivedFrom":subQ0}),-1.0]])]});}
            var Q80;
            {var subQ0=sQuery(id+"F0.wireOp",EDGE,"E29.1.14");var subQ1=sQuery(id+"F0.wireOp",EDGE,"E29.1.10");var subQ2=makeQuery(id+"F0.imprint","INTERSECT",VERTEX,{"disambiguationData":[OD(1.0)],"derivedFrom":[subQ1,subQ0]});Q80=makeQuery(id+"F0.imprint","IMPRINT",FACE,{"disambiguationData":[TD([[makeQuery(id+"F0.imprint","IMPRINT",EDGE,{"disambiguationData":[TD([[subQ2,-1.0]])],"derivedFrom":subQ1}),1.0]])]});}
            var Q81;
            {var subQ0=sQuery(id+"F0.wireOp",EDGE,"E29.1.14");var subQ1=sQuery(id+"F0.wireOp",EDGE,"E29.1.11");var subQ2=makeQuery(id+"F0.imprint","INTERSECT",VERTEX,{"disambiguationData":[OD(1.0)],"derivedFrom":[subQ1,subQ0]});Q81=makeQuery(id+"F0.imprint","IMPRINT",FACE,{"disambiguationData":[TD([[makeQuery(id+"F0.imprint","IMPRINT",EDGE,{"disambiguationData":[TD([[subQ2,-1.0]])],"derivedFrom":subQ1}),1.0]])]});}
            var Q82;
            {var subQ0=sQuery(id+"F0.wireOp",EDGE,"E29.1.12");var subQ1=sQuery(id+"F0.wireOp",EDGE,"E29.1.11");var subQ2=makeQuery(id+"F0.imprint","INTERSECT",VERTEX,{"disambiguationData":[OD(1.0)],"derivedFrom":[subQ1,subQ0]});Q82=makeQuery(id+"F0.imprint","IMPRINT",FACE,{"disambiguationData":[TD([[makeQuery(id+"F0.imprint","IMPRINT",EDGE,{"disambiguationData":[TD([[subQ2,-1.0]])],"derivedFrom":subQ1}),1.0]])]});}
            var Q83;
            {var subQ0=sQuery(id+"F0.wireOp",EDGE,"E29.2.5");var subQ1=sQuery(id+"F0.wireOp",EDGE,"E29.2.4");var subQ2=makeQuery(id+"F0.imprint","INTERSECT",VERTEX,{"disambiguationData":[OD(0.0)],"derivedFrom":[subQ1,subQ0]});Q83=makeQuery(id+"F0.imprint","IMPRINT",FACE,{"disambiguationData":[TD([[makeQuery(id+"F0.imprint","IMPRINT",EDGE,{"disambiguationData":[TD([[subQ2,1.0]])],"derivedFrom":subQ1}),1.0]])]});}
            var Q84;
            {var subQ0=sQuery(id+"F0.wireOp",EDGE,"E29.2.5");var subQ1=sQuery(id+"F0.wireOp",EDGE,"E29.2.4");var subQ2=makeQuery(id+"F0.imprint","INTERSECT",VERTEX,{"disambiguationData":[OD(0.0)],"derivedFrom":[subQ1,subQ0]});Q84=makeQuery(id+"F0.imprint","IMPRINT",FACE,{"disambiguationData":[TD([[makeQuery(id+"F0.imprint","IMPRINT",EDGE,{"disambiguationData":[TD([[subQ2,-1.0]])],"derivedFrom":subQ1}),1.0]])]});}
            var Q85;
            {var subQ0=sQuery(id+"F0.wireOp",EDGE,"E29.2.7");var subQ1=sQuery(id+"F0.wireOp",EDGE,"E29.2.3");var subQ2=makeQuery(id+"F0.imprint","INTERSECT",VERTEX,{"disambiguationData":[OD(0.0)],"derivedFrom":[subQ1,subQ0]});Q85=makeQuery(id+"F0.imprint","IMPRINT",FACE,{"disambiguationData":[TD([[makeQuery(id+"F0.imprint","IMPRINT",EDGE,{"disambiguationData":[TD([[subQ2,-1.0]])],"derivedFrom":subQ1}),1.0]])]});}
            var Q86;
            {var subQ0=sQuery(id+"F0.wireOp",EDGE,"E29.2.5");var subQ1=sQuery(id+"F0.wireOp",EDGE,"E29.2.3");var subQ2=makeQuery(id+"F0.imprint","INTERSECT",VERTEX,{"disambiguationData":[OD(0.0)],"derivedFrom":[subQ1,subQ0]});Q86=makeQuery(id+"F0.imprint","IMPRINT",FACE,{"disambiguationData":[TD([[makeQuery(id+"F0.imprint","IMPRINT",EDGE,{"disambiguationData":[TD([[subQ2,-1.0]])],"derivedFrom":subQ1}),1.0]])]});}
            var Q87;
            {var subQ0=sQuery(id+"F0.wireOp",EDGE,"E29.2.6");var subQ1=sQuery(id+"F0.wireOp",EDGE,"E29.2.3");var subQ2=makeQuery(id+"F0.imprint","INTERSECT",VERTEX,{"disambiguationData":[OD(0.0)],"derivedFrom":[subQ1,subQ0]});Q87=makeQuery(id+"F0.imprint","IMPRINT",FACE,{"disambiguationData":[TD([[makeQuery(id+"F0.imprint","IMPRINT",EDGE,{"disambiguationData":[TD([[subQ2,1.0]])],"derivedFrom":subQ1}),1.0]])]});}
            var Q88;
            {var subQ0=sQuery(id+"F0.wireOp",EDGE,"E29.2.6");var subQ1=sQuery(id+"F0.wireOp",EDGE,"E29.2.4");var subQ2=makeQuery(id+"F0.imprint","INTERSECT",VERTEX,{"disambiguationData":[OD(0.0)],"derivedFrom":[subQ1,subQ0]});Q88=makeQuery(id+"F0.imprint","IMPRINT",FACE,{"disambiguationData":[TD([[makeQuery(id+"F0.imprint","IMPRINT",EDGE,{"disambiguationData":[TD([[subQ2,1.0]])],"derivedFrom":subQ1}),1.0]])]});}
            var Q89;
            {var subQ0=sQuery(id+"F0.wireOp",EDGE,"E29.2.6");var subQ1=sQuery(id+"F0.wireOp",EDGE,"E29.2.3");var subQ2=makeQuery(id+"F0.imprint","INTERSECT",VERTEX,{"disambiguationData":[OD(0.0)],"derivedFrom":[subQ1,subQ0]});Q89=makeQuery(id+"F0.imprint","IMPRINT",FACE,{"disambiguationData":[TD([[makeQuery(id+"F0.imprint","IMPRINT",EDGE,{"disambiguationData":[TD([[subQ2,-1.0]])],"derivedFrom":subQ1}),1.0]])]});}
            var Q90;
            {var subQ0=sQuery(id+"F0.wireOp",EDGE,"E29.2.7");var subQ1=sQuery(id+"F0.wireOp",EDGE,"E29.2.5");var subQ2=makeQuery(id+"F0.imprint","INTERSECT",VERTEX,{"disambiguationData":[OD(1.0)],"derivedFrom":[subQ1,subQ0]});Q90=makeQuery(id+"F0.imprint","IMPRINT",FACE,{"disambiguationData":[TD([[makeQuery(id+"F0.imprint","IMPRINT",EDGE,{"disambiguationData":[TD([[subQ2,-1.0]])],"derivedFrom":subQ1}),1.0]])]});}
            var Q91;
            {var subQ0=sQuery(id+"F0.wireOp",EDGE,"E29.2.7");var subQ1=sQuery(id+"F0.wireOp",EDGE,"E29.2.4");var subQ2=makeQuery(id+"F0.imprint","INTERSECT",VERTEX,{"disambiguationData":[OD(1.0)],"derivedFrom":[subQ1,subQ0]});Q91=makeQuery(id+"F0.imprint","IMPRINT",FACE,{"disambiguationData":[TD([[makeQuery(id+"F0.imprint","IMPRINT",EDGE,{"disambiguationData":[TD([[subQ2,-1.0]])],"derivedFrom":subQ1}),-1.0]])]});}
            var Q92;
            {var subQ0=sQuery(id+"F0.wireOp",EDGE,"E29.2.5");var subQ1=sQuery(id+"F0.wireOp",EDGE,"E29.2.4");var subQ2=makeQuery(id+"F0.imprint","INTERSECT",VERTEX,{"disambiguationData":[OD(0.0)],"derivedFrom":[subQ1,subQ0]});Q92=makeQuery(id+"F0.imprint","IMPRINT",FACE,{"disambiguationData":[TD([[makeQuery(id+"F0.imprint","IMPRINT",EDGE,{"disambiguationData":[TD([[subQ2,-1.0]])],"derivedFrom":subQ1}),-1.0]])]});}
            var Q93;
            {var subQ0=sQuery(id+"F0.wireOp",EDGE,"E29.2.6");var subQ1=sQuery(id+"F0.wireOp",EDGE,"E29.2.3");var subQ2=makeQuery(id+"F0.imprint","INTERSECT",VERTEX,{"disambiguationData":[OD(0.0)],"derivedFrom":[subQ1,subQ0]});Q93=makeQuery(id+"F0.imprint","IMPRINT",FACE,{"disambiguationData":[TD([[makeQuery(id+"F0.imprint","IMPRINT",EDGE,{"disambiguationData":[TD([[subQ2,1.0]])],"derivedFrom":subQ1}),-1.0]])]});}
            var Q94;
            {var subQ0=sQuery(id+"F0.wireOp",EDGE,"E29.2.5");var subQ1=sQuery(id+"F0.wireOp",EDGE,"E29.2.4");var subQ2=makeQuery(id+"F0.imprint","INTERSECT",VERTEX,{"disambiguationData":[OD(1.0)],"derivedFrom":[subQ1,subQ0]});Q94=makeQuery(id+"F0.imprint","IMPRINT",FACE,{"disambiguationData":[TD([[makeQuery(id+"F0.imprint","IMPRINT",EDGE,{"disambiguationData":[TD([[subQ2,-1.0]])],"derivedFrom":subQ1}),-1.0]])]});}
            var Q95;
            {var subQ0=sQuery(id+"F0.wireOp",EDGE,"E29.2.5");var subQ1=sQuery(id+"F0.wireOp",EDGE,"E29.2.4");var subQ2=makeQuery(id+"F0.imprint","INTERSECT",VERTEX,{"disambiguationData":[OD(0.0)],"derivedFrom":[subQ1,subQ0]});Q95=makeQuery(id+"F0.imprint","IMPRINT",FACE,{"disambiguationData":[TD([[makeQuery(id+"F0.imprint","IMPRINT",EDGE,{"disambiguationData":[TD([[subQ2,1.0]])],"derivedFrom":subQ1}),-1.0]])]});}
            var Q96;
            {var subQ0=sQuery(id+"F0.wireOp",EDGE,"E29.2.7");var subQ1=sQuery(id+"F0.wireOp",EDGE,"E29.2.3");var subQ2=makeQuery(id+"F0.imprint","INTERSECT",VERTEX,{"disambiguationData":[OD(1.0)],"derivedFrom":[subQ1,subQ0]});Q96=makeQuery(id+"F0.imprint","IMPRINT",FACE,{"disambiguationData":[TD([[makeQuery(id+"F0.imprint","IMPRINT",EDGE,{"disambiguationData":[TD([[subQ2,-1.0]])],"derivedFrom":subQ1}),-1.0]])]});}
            var Q97;
            {var subQ0=sQuery(id+"F0.wireOp",EDGE,"E29.2.6");var subQ1=sQuery(id+"F0.wireOp",EDGE,"E29.2.5");var subQ2=makeQuery(id+"F0.imprint","INTERSECT",VERTEX,{"disambiguationData":[OD(0.0)],"derivedFrom":[subQ1,subQ0]});Q97=makeQuery(id+"F0.imprint","IMPRINT",FACE,{"disambiguationData":[TD([[makeQuery(id+"F0.imprint","IMPRINT",EDGE,{"disambiguationData":[TD([[subQ2,-1.0]])],"derivedFrom":subQ1}),1.0]])]});}
            var Q98;
            {var subQ0=sQuery(id+"F0.wireOp",EDGE,"E29.2.5");var subQ1=sQuery(id+"F0.wireOp",EDGE,"E29.2.3");var subQ2=makeQuery(id+"F0.imprint","INTERSECT",VERTEX,{"disambiguationData":[OD(0.0)],"derivedFrom":[subQ1,subQ0]});Q98=makeQuery(id+"F0.imprint","IMPRINT",FACE,{"disambiguationData":[TD([[makeQuery(id+"F0.imprint","IMPRINT",EDGE,{"disambiguationData":[TD([[subQ2,-1.0]])],"derivedFrom":subQ1}),-1.0]])]});}
            var Q99;
            {var subQ0=sQuery(id+"F0.wireOp",EDGE,"E29.2.6");var subQ1=sQuery(id+"F0.wireOp",EDGE,"E29.2.3");var subQ2=makeQuery(id+"F0.imprint","INTERSECT",VERTEX,{"disambiguationData":[OD(0.0)],"derivedFrom":[subQ1,subQ0]});Q99=makeQuery(id+"F0.imprint","IMPRINT",FACE,{"disambiguationData":[TD([[makeQuery(id+"F0.imprint","IMPRINT",EDGE,{"disambiguationData":[TD([[subQ2,-1.0]])],"derivedFrom":subQ1}),-1.0]])]});}
            var Q100;
            {var subQ0=sQuery(id+"F0.wireOp",EDGE,"E29.2.4");var subQ1=sQuery(id+"F0.wireOp",EDGE,"E29.2.3");var subQ2=makeQuery(id+"F0.imprint","INTERSECT",VERTEX,{"derivedFrom":[subQ1,subQ0]});Q100=makeQuery(id+"F0.imprint","IMPRINT",FACE,{"disambiguationData":[TD([[makeQuery(id+"F0.imprint","IMPRINT",EDGE,{"disambiguationData":[TD([[subQ2,1.0]])],"derivedFrom":subQ1}),-1.0]])]});}
            var Q101;
            {var subQ0=sQuery(id+"F0.wireOp",EDGE,"E29.2.4");var subQ1=makeQuery(id+"F0.imprint","INTERSECT",VERTEX,{"derivedFrom":[sQuery(id+"F0.wireOp",EDGE,"E29.2.3"),subQ0]});Q101=makeQuery(id+"F0.imprint","IMPRINT",FACE,{"disambiguationData":[TD([[makeQuery(id+"F0.imprint","IMPRINT",EDGE,{"disambiguationData":[TD([[subQ1,1.0]])],"derivedFrom":subQ0}),1.0]])]});}
            var Q102;
            {var subQ0=sQuery(id+"F0.wireOp",EDGE,"E29.2.5");var subQ1=sQuery(id+"F0.wireOp",EDGE,"E29.2.3");var subQ2=makeQuery(id+"F0.imprint","INTERSECT",VERTEX,{"disambiguationData":[OD(1.0)],"derivedFrom":[subQ1,subQ0]});Q102=makeQuery(id+"F0.imprint","IMPRINT",FACE,{"disambiguationData":[TD([[makeQuery(id+"F0.imprint","IMPRINT",EDGE,{"disambiguationData":[TD([[subQ2,-1.0]])],"derivedFrom":subQ1}),-1.0]])]});}
            var Q103;
            {var subQ0=sQuery(id+"F0.wireOp",EDGE,"E29.2.12");var subQ1=sQuery(id+"F0.wireOp",EDGE,"E29.2.11");var subQ2=makeQuery(id+"F0.imprint","INTERSECT",VERTEX,{"disambiguationData":[OD(0.0)],"derivedFrom":[subQ1,subQ0]});Q103=makeQuery(id+"F0.imprint","IMPRINT",FACE,{"disambiguationData":[TD([[makeQuery(id+"F0.imprint","IMPRINT",EDGE,{"disambiguationData":[TD([[subQ2,-1.0]])],"derivedFrom":subQ1}),-1.0]])]});}
            var Q104;
            {var subQ0=sQuery(id+"F0.wireOp",EDGE,"E29.2.13");var subQ1=sQuery(id+"F0.wireOp",EDGE,"E29.2.10");var subQ2=makeQuery(id+"F0.imprint","INTERSECT",VERTEX,{"disambiguationData":[OD(0.0)],"derivedFrom":[subQ1,subQ0]});Q104=makeQuery(id+"F0.imprint","IMPRINT",FACE,{"disambiguationData":[TD([[makeQuery(id+"F0.imprint","IMPRINT",EDGE,{"disambiguationData":[TD([[subQ2,1.0]])],"derivedFrom":subQ1}),-1.0]])]});}
            var Q105;
            {var subQ0=sQuery(id+"F0.wireOp",EDGE,"E29.2.12");var subQ1=sQuery(id+"F0.wireOp",EDGE,"E29.2.10");var subQ2=makeQuery(id+"F0.imprint","INTERSECT",VERTEX,{"disambiguationData":[OD(0.0)],"derivedFrom":[subQ1,subQ0]});Q105=makeQuery(id+"F0.imprint","IMPRINT",FACE,{"disambiguationData":[TD([[makeQuery(id+"F0.imprint","IMPRINT",EDGE,{"disambiguationData":[TD([[subQ2,1.0]])],"derivedFrom":subQ1}),-1.0]])]});}
            var Q106;
            {var subQ0=sQuery(id+"F0.wireOp",EDGE,"E29.2.14");var subQ1=sQuery(id+"F0.wireOp",EDGE,"E29.2.11");var subQ2=makeQuery(id+"F0.imprint","INTERSECT",VERTEX,{"disambiguationData":[OD(0.0)],"derivedFrom":[subQ1,subQ0]});Q106=makeQuery(id+"F0.imprint","IMPRINT",FACE,{"disambiguationData":[TD([[makeQuery(id+"F0.imprint","IMPRINT",EDGE,{"disambiguationData":[TD([[subQ2,-1.0]])],"derivedFrom":subQ1}),-1.0]])]});}
            var Q107;
            {var subQ0=sQuery(id+"F0.wireOp",EDGE,"E29.2.13");var subQ1=sQuery(id+"F0.wireOp",EDGE,"E29.2.11");var subQ2=makeQuery(id+"F0.imprint","INTERSECT",VERTEX,{"disambiguationData":[OD(0.0)],"derivedFrom":[subQ1,subQ0]});Q107=makeQuery(id+"F0.imprint","IMPRINT",FACE,{"disambiguationData":[TD([[makeQuery(id+"F0.imprint","IMPRINT",EDGE,{"disambiguationData":[TD([[subQ2,-1.0]])],"derivedFrom":subQ1}),-1.0]])]});}
            var Q108;
            {var subQ0=sQuery(id+"F0.wireOp",EDGE,"E29.2.11");var subQ1=makeQuery(id+"F0.imprint","INTERSECT",VERTEX,{"derivedFrom":[sQuery(id+"F0.wireOp",EDGE,"E29.2.10"),subQ0]});Q108=makeQuery(id+"F0.imprint","IMPRINT",FACE,{"disambiguationData":[TD([[makeQuery(id+"F0.imprint","IMPRINT",EDGE,{"disambiguationData":[TD([[subQ1,-1.0]])],"derivedFrom":subQ0}),-1.0]])]});}
            var Q109;
            {var subQ0=sQuery(id+"F0.wireOp",EDGE,"E29.2.12");var subQ1=sQuery(id+"F0.wireOp",EDGE,"E29.2.10");var subQ2=makeQuery(id+"F0.imprint","INTERSECT",VERTEX,{"disambiguationData":[OD(0.0)],"derivedFrom":[subQ1,subQ0]});Q109=makeQuery(id+"F0.imprint","IMPRINT",FACE,{"disambiguationData":[TD([[makeQuery(id+"F0.imprint","IMPRINT",EDGE,{"disambiguationData":[TD([[subQ2,-1.0]])],"derivedFrom":subQ1}),-1.0]])]});}
            var Q110;
            {var subQ0=sQuery(id+"F0.wireOp",EDGE,"E29.2.12");var subQ1=sQuery(id+"F0.wireOp",EDGE,"E29.2.10");var subQ2=makeQuery(id+"F0.imprint","INTERSECT",VERTEX,{"disambiguationData":[OD(1.0)],"derivedFrom":[subQ1,subQ0]});Q110=makeQuery(id+"F0.imprint","IMPRINT",FACE,{"disambiguationData":[TD([[makeQuery(id+"F0.imprint","IMPRINT",EDGE,{"disambiguationData":[TD([[subQ2,-1.0]])],"derivedFrom":subQ1}),1.0]])]});}
            var Q111;
            {var subQ0=sQuery(id+"F0.wireOp",EDGE,"E29.2.12");var subQ1=sQuery(id+"F0.wireOp",EDGE,"E29.2.10");var subQ2=makeQuery(id+"F0.imprint","INTERSECT",VERTEX,{"disambiguationData":[OD(0.0)],"derivedFrom":[subQ1,subQ0]});Q111=makeQuery(id+"F0.imprint","IMPRINT",FACE,{"disambiguationData":[TD([[makeQuery(id+"F0.imprint","IMPRINT",EDGE,{"disambiguationData":[TD([[subQ2,1.0]])],"derivedFrom":subQ1}),1.0]])]});}
            var Q112;
            {var subQ0=sQuery(id+"F0.wireOp",EDGE,"E29.2.12");var subQ1=sQuery(id+"F0.wireOp",EDGE,"E29.2.11");var subQ2=makeQuery(id+"F0.imprint","INTERSECT",VERTEX,{"disambiguationData":[OD(0.0)],"derivedFrom":[subQ1,subQ0]});Q112=makeQuery(id+"F0.imprint","IMPRINT",FACE,{"disambiguationData":[TD([[makeQuery(id+"F0.imprint","IMPRINT",EDGE,{"disambiguationData":[TD([[subQ2,-1.0]])],"derivedFrom":subQ1}),1.0]])]});}
            var Q113;
            {var subQ0=sQuery(id+"F0.wireOp",EDGE,"E29.2.14");var subQ1=sQuery(id+"F0.wireOp",EDGE,"E29.2.12");var subQ2=makeQuery(id+"F0.imprint","INTERSECT",VERTEX,{"disambiguationData":[OD(1.0)],"derivedFrom":[subQ1,subQ0]});Q113=makeQuery(id+"F0.imprint","IMPRINT",FACE,{"disambiguationData":[TD([[makeQuery(id+"F0.imprint","IMPRINT",EDGE,{"disambiguationData":[TD([[subQ2,-1.0]])],"derivedFrom":subQ1}),-1.0]])]});}
            var Q114;
            {var subQ0=sQuery(id+"F0.wireOp",EDGE,"E29.2.11");var subQ1=sQuery(id+"F0.wireOp",EDGE,"E29.2.10");var subQ2=makeQuery(id+"F0.imprint","INTERSECT",VERTEX,{"derivedFrom":[subQ1,subQ0]});Q114=makeQuery(id+"F0.imprint","IMPRINT",FACE,{"disambiguationData":[TD([[makeQuery(id+"F0.imprint","IMPRINT",EDGE,{"disambiguationData":[TD([[subQ2,-1.0]])],"derivedFrom":subQ1}),1.0]])]});}
            var Q115;
            {var subQ0=sQuery(id+"F0.wireOp",EDGE,"E29.2.14");var subQ1=sQuery(id+"F0.wireOp",EDGE,"E29.2.11");var subQ2=makeQuery(id+"F0.imprint","INTERSECT",VERTEX,{"disambiguationData":[OD(1.0)],"derivedFrom":[subQ1,subQ0]});Q115=makeQuery(id+"F0.imprint","IMPRINT",FACE,{"disambiguationData":[TD([[makeQuery(id+"F0.imprint","IMPRINT",EDGE,{"disambiguationData":[TD([[subQ2,-1.0]])],"derivedFrom":subQ1}),1.0]])]});}
            var Q116;
            {var subQ0=sQuery(id+"F0.wireOp",EDGE,"E29.2.12");var subQ1=sQuery(id+"F0.wireOp",EDGE,"E29.2.10");var subQ2=makeQuery(id+"F0.imprint","INTERSECT",VERTEX,{"disambiguationData":[OD(0.0)],"derivedFrom":[subQ1,subQ0]});Q116=makeQuery(id+"F0.imprint","IMPRINT",FACE,{"disambiguationData":[TD([[makeQuery(id+"F0.imprint","IMPRINT",EDGE,{"disambiguationData":[TD([[subQ2,-1.0]])],"derivedFrom":subQ1}),1.0]])]});}
            var Q117;
            {var subQ0=sQuery(id+"F0.wireOp",EDGE,"E29.2.12");var subQ1=sQuery(id+"F0.wireOp",EDGE,"E29.2.11");var subQ2=makeQuery(id+"F0.imprint","INTERSECT",VERTEX,{"disambiguationData":[OD(1.0)],"derivedFrom":[subQ1,subQ0]});Q117=makeQuery(id+"F0.imprint","IMPRINT",FACE,{"disambiguationData":[TD([[makeQuery(id+"F0.imprint","IMPRINT",EDGE,{"disambiguationData":[TD([[subQ2,-1.0]])],"derivedFrom":subQ1}),1.0]])]});}
            var Q118;
            {var subQ0=sQuery(id+"F0.wireOp",EDGE,"E29.2.14");var subQ1=sQuery(id+"F0.wireOp",EDGE,"E29.2.10");var subQ2=makeQuery(id+"F0.imprint","INTERSECT",VERTEX,{"disambiguationData":[OD(0.0)],"derivedFrom":[subQ1,subQ0]});Q118=makeQuery(id+"F0.imprint","IMPRINT",FACE,{"disambiguationData":[TD([[makeQuery(id+"F0.imprint","IMPRINT",EDGE,{"disambiguationData":[TD([[subQ2,-1.0]])],"derivedFrom":subQ1}),-1.0]])]});}
            var Q119;
            {var subQ0=sQuery(id+"F0.wireOp",EDGE,"E29.2.13");var subQ1=sQuery(id+"F0.wireOp",EDGE,"E29.2.12");var subQ2=makeQuery(id+"F0.imprint","INTERSECT",VERTEX,{"disambiguationData":[OD(0.0)],"derivedFrom":[subQ1,subQ0]});Q119=makeQuery(id+"F0.imprint","IMPRINT",FACE,{"disambiguationData":[TD([[makeQuery(id+"F0.imprint","IMPRINT",EDGE,{"disambiguationData":[TD([[subQ2,-1.0]])],"derivedFrom":subQ1}),-1.0]])]});}
            var Q120;
            {var subQ0=sQuery(id+"F0.wireOp",EDGE,"E29.2.14");var subQ1=sQuery(id+"F0.wireOp",EDGE,"E29.2.10");var subQ2=makeQuery(id+"F0.imprint","INTERSECT",VERTEX,{"disambiguationData":[OD(0.0)],"derivedFrom":[subQ1,subQ0]});Q120=makeQuery(id+"F0.imprint","IMPRINT",FACE,{"disambiguationData":[TD([[makeQuery(id+"F0.imprint","IMPRINT",EDGE,{"disambiguationData":[TD([[subQ2,-1.0]])],"derivedFrom":subQ1}),1.0]])]});}
            var Q121;
            {var subQ0=sQuery(id+"F0.wireOp",EDGE,"E29.2.13");var subQ1=sQuery(id+"F0.wireOp",EDGE,"E29.2.11");var subQ2=makeQuery(id+"F0.imprint","INTERSECT",VERTEX,{"disambiguationData":[OD(0.0)],"derivedFrom":[subQ1,subQ0]});Q121=makeQuery(id+"F0.imprint","IMPRINT",FACE,{"disambiguationData":[TD([[makeQuery(id+"F0.imprint","IMPRINT",EDGE,{"disambiguationData":[TD([[subQ2,-1.0]])],"derivedFrom":subQ1}),1.0]])]});}
            var Q122;
            {var subQ0=sQuery(id+"F0.wireOp",EDGE,"E29.2.14");var subQ1=sQuery(id+"F0.wireOp",EDGE,"E29.2.10");var subQ2=makeQuery(id+"F0.imprint","INTERSECT",VERTEX,{"disambiguationData":[OD(1.0)],"derivedFrom":[subQ1,subQ0]});Q122=makeQuery(id+"F0.imprint","IMPRINT",FACE,{"disambiguationData":[TD([[makeQuery(id+"F0.imprint","IMPRINT",EDGE,{"disambiguationData":[TD([[subQ2,-1.0]])],"derivedFrom":subQ1}),1.0]])]});}
            var Q123;
            {var subQ13=sQuery(id+"F0.wireOp",EDGE,"E1.2.3");Q123=makeQuery(id+"F0.imprint","IMPRINT",FACE,{"disambiguationData":[TD([[makeQuery(id+"F0.imprint","IMPRINT",EDGE,{"derivedFrom":subQ13}),-1.0]])]});}
            var Q124;
            {var subQ0=sQuery(id+"F0.wireOp",EDGE,"8HJL9n9t-ZLUA-CEe9-PNdE-h4bfHI8nPg3d");var subQ1=sQuery(id+"F0.wireOp",EDGE,"E1.2.2");var subQ2=makeQuery(id+"F0.imprint","INTERSECT",VERTEX,{"disambiguationData":[OD(0.0)],"derivedFrom":[subQ1,subQ0]});Q124=makeQuery(id+"F0.imprint","IMPRINT",FACE,{"disambiguationData":[TD([[makeQuery(id+"F0.imprint","IMPRINT",EDGE,{"disambiguationData":[TD([[subQ2,-1.0]])],"derivedFrom":subQ1}),1.0]])]});}
            var Q125;
            {var subQ12=sQuery(id+"F0.wireOp",EDGE,"E1.2.0");Q125=makeQuery(id+"F0.imprint","IMPRINT",FACE,{"disambiguationData":[TD([[makeQuery(id+"F0.imprint","IMPRINT",EDGE,{"derivedFrom":subQ12}),1.0]])]});}
            var Q126;
            {var subQ3=sQuery(id+"F0.wireOp",EDGE,"E1.1.3");Q126=makeQuery(id+"F0.imprint","IMPRINT",FACE,{"disambiguationData":[TD([[makeQuery(id+"F0.imprint","IMPRINT",EDGE,{"derivedFrom":subQ3}),1.0]])]});}
            var Q127;
            {var subQ0=sQuery(id+"F0.wireOp",EDGE,"E29.2.1");Q127=makeQuery(id+"F0.imprint","IMPRINT",FACE,{"disambiguationData":[TD([[makeQuery(id+"F0.imprint","IMPRINT",EDGE,{"derivedFrom":subQ0}),-1.0]])]});}
            var Q128;
            {var subQ4=sQuery(id+"F0.wireOp",EDGE,"gPkFda2c-Dm8t-b8RN-PjmV-kEG28G5E5dCk");var subQ5=sQuery(id+"F0.wireOp",EDGE,"E0.bottom");var subQ9=makeQuery(id+"F0.imprint","INTERSECT",VERTEX,{"disambiguationData":[OD(0.0)],"derivedFrom":[subQ5,subQ4]});Q128=makeQuery(id+"F0.imprint","IMPRINT",FACE,{"disambiguationData":[TD([[makeQuery(id+"F0.imprint","IMPRINT",EDGE,{"disambiguationData":[TD([[subQ9,-1.0]])],"derivedFrom":subQ5}),1.0]])]});}
            var Q129;
            {var subQ0=sQuery(id+"F0.wireOp",EDGE,"db7fad64-9b78-43cb-8bcf-14bc5c4bf4ee.trimOffspring");Q129=makeQuery(id+"F0.imprint","IMPRINT",FACE,{"disambiguationData":[TD([[makeQuery(id+"F0.imprint","IMPRINT",EDGE,{"derivedFrom":subQ0}),1.0]])]});}
            var Q130;
            {var subQ0=sQuery(id+"F0.wireOp",EDGE,"7417e1bb-57cb-4ff5-af8a-17b651de926c.1.0");Q130=makeQuery(id+"F0.imprint","IMPRINT",FACE,{"disambiguationData":[TD([[makeQuery(id+"F0.imprint","IMPRINT",EDGE,{"derivedFrom":subQ0}),1.0]])]});}
            var Q131;
            {var subQ0=sQuery(id+"F0.wireOp",EDGE,"7417e1bb-57cb-4ff5-af8a-17b651de926c.2.0");Q131=makeQuery(id+"F0.imprint","IMPRINT",FACE,{"disambiguationData":[TD([[makeQuery(id+"F0.imprint","IMPRINT",EDGE,{"derivedFrom":subQ0}),1.0]])]});}
            var Q132;
            {var subQ4=sQuery(id+"F0.wireOp",EDGE,"7417e1bb-57cb-4ff5-af8a-17b651de926c.2.0");var subQ5=sQuery(id+"F0.wireOp",EDGE,"E1.1.1");var subQ8=makeQuery(id+"F0.imprint","INTERSECT",VERTEX,{"disambiguationData":[OD(1.0)],"derivedFrom":[subQ5,subQ4]});Q132=makeQuery(id+"F0.imprint","IMPRINT",FACE,{"disambiguationData":[TD([[makeQuery(id+"F0.imprint","IMPRINT",EDGE,{"disambiguationData":[TD([[subQ8,1.0]])],"derivedFrom":subQ5}),-1.0]])]});}
            var Q133;
            {var subQ0=sQuery(id+"F0.wireOp",EDGE,"3KDm2ICS-a2cK-OPck-MTX1-qhdp1wuGhW6i");Q133=makeQuery(id+"F0.imprint","IMPRINT",FACE,{"disambiguationData":[TD([[makeQuery(id+"F0.imprint","IMPRINT",EDGE,{"derivedFrom":subQ0}),-1.0]])]});}
            var Q134;
            {var subQ4=sQuery(id+"F0.wireOp",EDGE,"E1.2.1");var subQ6=sQuery(id+"F0.wireOp",EDGE,"db7fad64-9b78-43cb-8bcf-14bc5c4bf4ee.trimOffspring");var subQ9=makeQuery(id+"F0.imprint","INTERSECT",VERTEX,{"disambiguationData":[OD(1.0)],"derivedFrom":[subQ4,subQ6]});Q134=makeQuery(id+"F0.imprint","IMPRINT",FACE,{"disambiguationData":[TD([[makeQuery(id+"F0.imprint","IMPRINT",EDGE,{"disambiguationData":[TD([[subQ9,1.0]])],"derivedFrom":subQ4}),-1.0]])]});}
            var Q135;
            {var subQ0=sQuery(id+"F0.wireOp",EDGE,"8HJL9n9t-ZLUA-CEe9-PNdE-h4bfHI8nPg3d");var subQ1=sQuery(id+"F0.wireOp",EDGE,"E1.2.1");var subQ2=makeQuery(id+"F0.imprint","INTERSECT",VERTEX,{"disambiguationData":[OD(1.0)],"derivedFrom":[subQ1,subQ0]});Q135=makeQuery(id+"F0.imprint","IMPRINT",FACE,{"disambiguationData":[TD([[makeQuery(id+"F0.imprint","IMPRINT",EDGE,{"disambiguationData":[TD([[subQ2,-1.0]])],"derivedFrom":subQ1}),-1.0]])]});}
            var Q136;
            {var subQ0=sQuery(id+"F0.wireOp",EDGE,"gPkFda2c-Dm8t-b8RN-PjmV-kEG28G5E5dCk");var subQ1=sQuery(id+"F0.wireOp",EDGE,"E1.2.1");var subQ2=makeQuery(id+"F0.imprint","INTERSECT",VERTEX,{"disambiguationData":[OD(0.0)],"derivedFrom":[subQ1,subQ0]});Q136=makeQuery(id+"F0.imprint","IMPRINT",FACE,{"disambiguationData":[TD([[makeQuery(id+"F0.imprint","IMPRINT",EDGE,{"disambiguationData":[TD([[subQ2,-1.0]])],"derivedFrom":subQ1}),-1.0]])]});}
            var Q137;
            {var subQ3=sQuery(id+"F0.wireOp",EDGE,"E0.left");Q137=makeQuery(id+"F0.imprint","IMPRINT",FACE,{"disambiguationData":[TD([[makeQuery(id+"F0.imprint","IMPRINT",EDGE,{"derivedFrom":subQ3}),-1.0]])]});}
            var Q138;
            {var subQ9=sQuery(id+"F0.wireOp",EDGE,"E0.left");Q138=makeQuery(id+"F0.imprint","IMPRINT",FACE,{"disambiguationData":[TD([[makeQuery(id+"F0.imprint","IMPRINT",EDGE,{"derivedFrom":subQ9}),1.0]])]});}
            var Q139;
            {var subQ0=sQuery(id+"F0.wireOp",EDGE,"7417e1bb-57cb-4ff5-af8a-17b651de926c.1.0");var subQ1=sQuery(id+"F0.wireOp",EDGE,"E0.bottom");var subQ8=makeQuery(id+"F0.imprint","INTERSECT",VERTEX,{"disambiguationData":[OD(1.0)],"derivedFrom":[subQ1,subQ0]});Q139=makeQuery(id+"F0.imprint","IMPRINT",FACE,{"disambiguationData":[TD([[makeQuery(id+"F0.imprint","IMPRINT",EDGE,{"disambiguationData":[TD([[subQ8,1.0]])],"derivedFrom":subQ1}),-1.0]])]});}
            var Q140;
            {var subQ0=sQuery(id+"F0.wireOp",EDGE,"gPkFda2c-Dm8t-b8RN-PjmV-kEG28G5E5dCk");var subQ1=sQuery(id+"F0.wireOp",EDGE,"E0.bottom");var subQ2=makeQuery(id+"F0.imprint","INTERSECT",VERTEX,{"disambiguationData":[OD(0.0)],"derivedFrom":[subQ1,subQ0]});Q140=makeQuery(id+"F0.imprint","IMPRINT",FACE,{"disambiguationData":[TD([[makeQuery(id+"F0.imprint","IMPRINT",EDGE,{"disambiguationData":[TD([[subQ2,-1.0]])],"derivedFrom":subQ1}),-1.0]])]});}
            var Q141;
            {var subQ0=sQuery(id+"F0.wireOp",EDGE,"E29.1.0");var subQ1=sQuery(id+"F0.wireOp",EDGE,"E0.bottom");var subQ2=makeQuery(id+"F0.imprint","INTERSECT",VERTEX,{"disambiguationData":[OD(1.0)],"derivedFrom":[subQ1,subQ0]});Q141=makeQuery(id+"F0.imprint","IMPRINT",FACE,{"disambiguationData":[TD([[makeQuery(id+"F0.imprint","IMPRINT",EDGE,{"disambiguationData":[TD([[subQ2,-1.0]])],"derivedFrom":subQ1}),-1.0]])]});}
            var Q142;
            {var subQ0=sQuery(id+"F0.wireOp",EDGE,"E29.1.0");var subQ1=sQuery(id+"F0.wireOp",EDGE,"E0.top");var subQ2=makeQuery(id+"F0.imprint","INTERSECT",VERTEX,{"disambiguationData":[OD(0.0)],"derivedFrom":[subQ1,subQ0]});Q142=makeQuery(id+"F0.imprint","IMPRINT",FACE,{"disambiguationData":[TD([[makeQuery(id+"F0.imprint","IMPRINT",EDGE,{"disambiguationData":[TD([[subQ2,-1.0]])],"derivedFrom":subQ1}),1.0]])]});}
            var Q143;
            {var subQ5=sQuery(id+"F0.wireOp",EDGE,"E0.right");Q143=makeQuery(id+"F0.imprint","IMPRINT",FACE,{"disambiguationData":[TD([[makeQuery(id+"F0.imprint","IMPRINT",EDGE,{"derivedFrom":subQ5}),-1.0]])]});}
            var Q144;
            {var subQ0=sQuery(id+"F0.wireOp",EDGE,"gPkFda2c-Dm8t-b8RN-PjmV-kEG28G5E5dCk");var subQ1=sQuery(id+"F0.wireOp",EDGE,"E1.1.1");var subQ2=makeQuery(id+"F0.imprint","INTERSECT",VERTEX,{"disambiguationData":[OD(0.0)],"derivedFrom":[subQ1,subQ0]});Q144=makeQuery(id+"F0.imprint","IMPRINT",FACE,{"disambiguationData":[TD([[makeQuery(id+"F0.imprint","IMPRINT",EDGE,{"disambiguationData":[TD([[subQ2,-1.0]])],"derivedFrom":subQ1}),-1.0]])]});}
            var Q145;
            {var subQ0=sQuery(id+"F0.wireOp",EDGE,"E29.2.0");var subQ1=sQuery(id+"F0.wireOp",EDGE,"E1.1.1");var subQ2=makeQuery(id+"F0.imprint","INTERSECT",VERTEX,{"disambiguationData":[OD(1.0)],"derivedFrom":[subQ1,subQ0]});Q145=makeQuery(id+"F0.imprint","IMPRINT",FACE,{"disambiguationData":[TD([[makeQuery(id+"F0.imprint","IMPRINT",EDGE,{"disambiguationData":[TD([[subQ2,-1.0]])],"derivedFrom":subQ1}),-1.0]])]});}
            var Q146;
            {var subQ0=sQuery(id+"F0.wireOp",EDGE,"E29.1.1");Q146=makeQuery(id+"F0.imprint","IMPRINT",FACE,{"disambiguationData":[TD([[makeQuery(id+"F0.imprint","IMPRINT",EDGE,{"derivedFrom":subQ0}),-1.0]])]});}
            var Q147;
            {var subQ3=sQuery(id+"F0.wireOp",EDGE,"E0.right");Q147=makeQuery(id+"F0.imprint","IMPRINT",FACE,{"disambiguationData":[TD([[makeQuery(id+"F0.imprint","IMPRINT",EDGE,{"derivedFrom":subQ3}),1.0]])]});}
            var Q148;
            {var subQ0=sQuery(id+"F0.wireOp",EDGE,"8HJL9n9t-ZLUA-CEe9-PNdE-h4bfHI8nPg3d");var subQ1=sQuery(id+"F0.wireOp",EDGE,"E1.2.1");var subQ2=makeQuery(id+"F0.imprint","INTERSECT",VERTEX,{"disambiguationData":[OD(0.0)],"derivedFrom":[subQ1,subQ0]});Q148=makeQuery(id+"F0.imprint","IMPRINT",FACE,{"disambiguationData":[TD([[makeQuery(id+"F0.imprint","IMPRINT",EDGE,{"disambiguationData":[TD([[subQ2,-1.0]])],"derivedFrom":subQ1}),1.0]])]});}
            var Q149;
            {var subQ0=sQuery(id+"F0.wireOp",EDGE,"8HJL9n9t-ZLUA-CEe9-PNdE-h4bfHI8nPg3d");var subQ1=sQuery(id+"F0.wireOp",EDGE,"E1.2.1");var subQ2=makeQuery(id+"F0.imprint","INTERSECT",VERTEX,{"disambiguationData":[OD(0.0)],"derivedFrom":[subQ1,subQ0]});Q149=makeQuery(id+"F0.imprint","IMPRINT",FACE,{"disambiguationData":[TD([[makeQuery(id+"F0.imprint","IMPRINT",EDGE,{"disambiguationData":[TD([[subQ2,-1.0]])],"derivedFrom":subQ1}),-1.0]])]});}
            var Q150;
            {var subQ0=sQuery(id+"F0.wireOp",EDGE,"E29.1.0");var subQ1=sQuery(id+"F0.wireOp",EDGE,"E0.bottom");var subQ2=makeQuery(id+"F0.imprint","INTERSECT",VERTEX,{"disambiguationData":[OD(0.0)],"derivedFrom":[subQ1,subQ0]});Q150=makeQuery(id+"F0.imprint","IMPRINT",FACE,{"disambiguationData":[TD([[makeQuery(id+"F0.imprint","IMPRINT",EDGE,{"disambiguationData":[TD([[subQ2,-1.0]])],"derivedFrom":subQ1}),-1.0]])]});}
            var Q151;
            {var subQ0=sQuery(id+"F0.wireOp",EDGE,"E29.1.0");var subQ1=sQuery(id+"F0.wireOp",EDGE,"E0.bottom");var subQ2=makeQuery(id+"F0.imprint","INTERSECT",VERTEX,{"disambiguationData":[OD(0.0)],"derivedFrom":[subQ1,subQ0]});Q151=makeQuery(id+"F0.imprint","IMPRINT",FACE,{"disambiguationData":[TD([[makeQuery(id+"F0.imprint","IMPRINT",EDGE,{"disambiguationData":[TD([[subQ2,-1.0]])],"derivedFrom":subQ1}),1.0]])]});}
            var Q152;
            {var subQ0=sQuery(id+"F0.wireOp",EDGE,"E29.2.0");var subQ1=sQuery(id+"F0.wireOp",EDGE,"E1.1.1");var subQ2=makeQuery(id+"F0.imprint","INTERSECT",VERTEX,{"disambiguationData":[OD(0.0)],"derivedFrom":[subQ1,subQ0]});Q152=makeQuery(id+"F0.imprint","IMPRINT",FACE,{"disambiguationData":[TD([[makeQuery(id+"F0.imprint","IMPRINT",EDGE,{"disambiguationData":[TD([[subQ2,-1.0]])],"derivedFrom":subQ1}),1.0]])]});}
            var Q153;
            {var subQ0=sQuery(id+"F0.wireOp",EDGE,"E29.2.0");var subQ1=sQuery(id+"F0.wireOp",EDGE,"E1.1.1");var subQ2=makeQuery(id+"F0.imprint","INTERSECT",VERTEX,{"disambiguationData":[OD(0.0)],"derivedFrom":[subQ1,subQ0]});Q153=makeQuery(id+"F0.imprint","IMPRINT",FACE,{"disambiguationData":[TD([[makeQuery(id+"F0.imprint","IMPRINT",EDGE,{"disambiguationData":[TD([[subQ2,-1.0]])],"derivedFrom":subQ1}),-1.0]])]});}
            var Q154;
            Q154=sQuery(id+"F0.wireOp",EDGE,"E19");
            var Q155;
            Q155=sQuery(id+"F0.wireOp",EDGE,"E20.1.0.0");
            extrude(context, id + "F1", {"entities" : qUnion([Q0, Q1, Q2, Q3, Q4, Q5, Q6, Q7, Q8, Q9, Q10, Q11, Q12, Q13, Q14, Q15, Q16, Q17, Q18, Q19, Q20, Q21, Q22, Q23, Q24, Q25, Q26, Q27, Q28, Q29, Q30, Q31, Q32, Q33, Q34, Q35, Q36, Q37, Q38, Q39, Q40, Q41, Q42, Q43, Q44, Q45, Q46, Q47, Q48, Q49, Q50, Q51, Q52, Q53, Q54, Q55, Q56, Q57, Q58, Q59, Q60, Q61, Q62, Q63, Q64, Q65, Q66, Q67, Q68, Q69, Q70, Q71, Q72, Q73, Q74, Q75, Q76, Q77, Q78, Q79, Q80, Q81, Q82, Q83, Q84, Q85, Q86, Q87, Q88, Q89, Q90, Q91, Q92, Q93, Q94, Q95, Q96, Q97, Q98, Q99, Q100, Q101, Q102, Q103, Q104, Q105, Q106, Q107, Q108, Q109, Q110, Q111, Q112, Q113, Q114, Q115, Q116, Q117, Q118, Q119, Q120, Q121, Q122, Q123, Q124, Q125, Q126, Q127, Q128, Q129, Q130, Q131, Q132, Q133, Q134, Q135, Q136, Q137, Q138, Q139, Q140, Q141, Q142, Q143, Q144, Q145, Q146, Q147, Q148, Q149, Q150, Q151, Q152, Q153]), "surfaceEntities" : qUnion([Q154, Q155]), "depth" : 3 * mm});
        }
        {
            var Q0;
            Q0=makeQuery(id+"F1.opExtrude","SWEPT_BODY",BODY,{"disambiguationData":[OSD([sQuery(id+"F0.wireOp",EDGE,"E0.bottom"),sQuery(id+"F0.wireOp",EDGE,"E0.top"),sQuery(id+"F0.wireOp",EDGE,"E1.1.1"),sQuery(id+"F0.wireOp",EDGE,"E1.1.2"),sQuery(id+"F0.wireOp",EDGE,"E1.2.1"),sQuery(id+"F0.wireOp",EDGE,"E1.2.2"),sQuery(id+"F0.wireOp",EDGE,"E2"),sQuery(id+"F0.wireOp",EDGE,"E3"),sQuery(id+"F0.wireOp",EDGE,"E4"),sQuery(id+"F0.wireOp",EDGE,"kepUIwOW-SZzq-0WKR-rI8W-qkmqDNEbz00S"),sQuery(id+"F0.wireOp",EDGE,"db7fad64-9b78-43cb-8bcf-14bc5c4bf4ee.trimOffspring"),sQuery(id+"F0.wireOp",EDGE,"7417e1bb-57cb-4ff5-af8a-17b651de926c.1.0"),sQuery(id+"F0.wireOp",EDGE,"7417e1bb-57cb-4ff5-af8a-17b651de926c.2.0"),sQuery(id+"F0.wireOp",EDGE,"8HJL9n9t-ZLUA-CEe9-PNdE-h4bfHI8nPg3d"),sQuery(id+"F0.wireOp",EDGE,"eb3e8c90-a782-4fc0-a3a2-c71c6e8238640.MirrorC"),sQuery(id+"F0.wireOp",EDGE,"bbd128de-10de-47b4-830c-765d0eece995.1.0"),sQuery(id+"F0.wireOp",EDGE,"bbd128de-10de-47b4-830c-765d0eece995.1.2"),sQuery(id+"F0.wireOp",EDGE,"bbd128de-10de-47b4-830c-765d0eece995.2.0"),sQuery(id+"F0.wireOp",EDGE,"bbd128de-10de-47b4-830c-765d0eece995.2.2"),sQuery(id+"F0.wireOp",EDGE,"E24"),sQuery(id+"F0.wireOp",EDGE,"E29.1.0"),sQuery(id+"F0.wireOp",EDGE,"E29.1.2"),sQuery(id+"F0.wireOp",EDGE,"E29.2.0"),sQuery(id+"F0.wireOp",EDGE,"E29.2.2")])]});
            transform(context, id + "F2", {"entities" : qUnion([Q0]), "transformType" : TransformType.TRANSLATION_3D, "dx" : 0 * mm, "dy" : 0 * mm, "dz" : -130 * mm, "makeCopy" : false});
        }
        {
            var Q0;
            {var subQ4=sQuery(id+"F0.wireOp",EDGE,"gPkFda2c-Dm8t-b8RN-PjmV-kEG28G5E5dCk");var subQ5=sQuery(id+"F0.wireOp",EDGE,"E0.bottom");var subQ9=makeQuery(id+"F0.imprint","INTERSECT",VERTEX,{"disambiguationData":[OD(0.0)],"derivedFrom":[subQ5,subQ4]});Q0=makeQuery(id+"F0.imprint","IMPRINT",FACE,{"disambiguationData":[TD([[makeQuery(id+"F0.imprint","IMPRINT",EDGE,{"disambiguationData":[TD([[subQ9,-1.0]])],"derivedFrom":subQ5}),1.0]])]});}
            var Q1;
            {var subQ12=sQuery(id+"F0.wireOp",EDGE,"E1.2.0");Q1=makeQuery(id+"F0.imprint","IMPRINT",FACE,{"disambiguationData":[TD([[makeQuery(id+"F0.imprint","IMPRINT",EDGE,{"derivedFrom":subQ12}),1.0]])]});}
            var Q2;
            {var subQ0=sQuery(id+"F0.wireOp",EDGE,"E29.2.1");Q2=makeQuery(id+"F0.imprint","IMPRINT",FACE,{"disambiguationData":[TD([[makeQuery(id+"F0.imprint","IMPRINT",EDGE,{"derivedFrom":subQ0}),-1.0]])]});}
            var Q3;
            {var subQ7=sQuery(id+"F0.wireOp",EDGE,"E1.1.3");Q3=makeQuery(id+"F0.imprint","IMPRINT",FACE,{"disambiguationData":[TD([[makeQuery(id+"F0.imprint","IMPRINT",EDGE,{"derivedFrom":subQ7}),-1.0]])]});}
            var Q4;
            {var subQ0=sQuery(id+"F0.wireOp",EDGE,"gPkFda2c-Dm8t-b8RN-PjmV-kEG28G5E5dCk");var subQ1=sQuery(id+"F0.wireOp",EDGE,"E1.2.1");var subQ2=makeQuery(id+"F0.imprint","INTERSECT",VERTEX,{"disambiguationData":[OD(0.0)],"derivedFrom":[subQ1,subQ0]});Q4=makeQuery(id+"F0.imprint","IMPRINT",FACE,{"disambiguationData":[TD([[makeQuery(id+"F0.imprint","IMPRINT",EDGE,{"disambiguationData":[TD([[subQ2,-1.0]])],"derivedFrom":subQ1}),-1.0]])]});}
            var Q5;
            {var subQ0=sQuery(id+"F0.wireOp",EDGE,"E29.2.0");var subQ1=sQuery(id+"F0.wireOp",EDGE,"E1.1.1");var subQ2=makeQuery(id+"F0.imprint","INTERSECT",VERTEX,{"disambiguationData":[OD(1.0)],"derivedFrom":[subQ1,subQ0]});Q5=makeQuery(id+"F0.imprint","IMPRINT",FACE,{"disambiguationData":[TD([[makeQuery(id+"F0.imprint","IMPRINT",EDGE,{"disambiguationData":[TD([[subQ2,-1.0]])],"derivedFrom":subQ1}),-1.0]])]});}
            var Q6;
            {var subQ0=sQuery(id+"F0.wireOp",EDGE,"8HJL9n9t-ZLUA-CEe9-PNdE-h4bfHI8nPg3d");var subQ1=sQuery(id+"F0.wireOp",EDGE,"E1.2.1");var subQ2=makeQuery(id+"F0.imprint","INTERSECT",VERTEX,{"disambiguationData":[OD(1.0)],"derivedFrom":[subQ1,subQ0]});Q6=makeQuery(id+"F0.imprint","IMPRINT",FACE,{"disambiguationData":[TD([[makeQuery(id+"F0.imprint","IMPRINT",EDGE,{"disambiguationData":[TD([[subQ2,-1.0]])],"derivedFrom":subQ1}),-1.0]])]});}
            var Q7;
            {var subQ13=sQuery(id+"F0.wireOp",EDGE,"E1.2.3");Q7=makeQuery(id+"F0.imprint","IMPRINT",FACE,{"disambiguationData":[TD([[makeQuery(id+"F0.imprint","IMPRINT",EDGE,{"derivedFrom":subQ13}),-1.0]])]});}
            var Q8;
            {var subQ0=sQuery(id+"F0.wireOp",EDGE,"3KDm2ICS-a2cK-OPck-MTX1-qhdp1wuGhW6i");Q8=makeQuery(id+"F0.imprint","IMPRINT",FACE,{"disambiguationData":[TD([[makeQuery(id+"F0.imprint","IMPRINT",EDGE,{"derivedFrom":subQ0}),-1.0]])]});}
            var Q9;
            {var subQ0=sQuery(id+"F0.wireOp",EDGE,"gPkFda2c-Dm8t-b8RN-PjmV-kEG28G5E5dCk");var subQ1=sQuery(id+"F0.wireOp",EDGE,"E1.1.1");var subQ2=makeQuery(id+"F0.imprint","INTERSECT",VERTEX,{"disambiguationData":[OD(0.0)],"derivedFrom":[subQ1,subQ0]});Q9=makeQuery(id+"F0.imprint","IMPRINT",FACE,{"disambiguationData":[TD([[makeQuery(id+"F0.imprint","IMPRINT",EDGE,{"disambiguationData":[TD([[subQ2,-1.0]])],"derivedFrom":subQ1}),-1.0]])]});}
            var Q10;
            {var subQ19=sQuery(id+"F0.wireOp",EDGE,"E1.1.0");Q10=makeQuery(id+"F0.imprint","IMPRINT",FACE,{"disambiguationData":[TD([[makeQuery(id+"F0.imprint","IMPRINT",EDGE,{"derivedFrom":subQ19}),1.0]])]});}
            var Q11;
            {var subQ0=sQuery(id+"F0.wireOp",EDGE,"E29.1.1");Q11=makeQuery(id+"F0.imprint","IMPRINT",FACE,{"disambiguationData":[TD([[makeQuery(id+"F0.imprint","IMPRINT",EDGE,{"derivedFrom":subQ0}),-1.0]])]});}
            var Q12;
            {var subQ5=sQuery(id+"F0.wireOp",EDGE,"E0.right");Q12=makeQuery(id+"F0.imprint","IMPRINT",FACE,{"disambiguationData":[TD([[makeQuery(id+"F0.imprint","IMPRINT",EDGE,{"derivedFrom":subQ5}),-1.0]])]});}
            var Q13;
            {var subQ0=sQuery(id+"F0.wireOp",EDGE,"E29.1.0");var subQ1=sQuery(id+"F0.wireOp",EDGE,"E0.bottom");var subQ2=makeQuery(id+"F0.imprint","INTERSECT",VERTEX,{"disambiguationData":[OD(1.0)],"derivedFrom":[subQ1,subQ0]});Q13=makeQuery(id+"F0.imprint","IMPRINT",FACE,{"disambiguationData":[TD([[makeQuery(id+"F0.imprint","IMPRINT",EDGE,{"disambiguationData":[TD([[subQ2,-1.0]])],"derivedFrom":subQ1}),-1.0]])]});}
            var Q14;
            {var subQ9=sQuery(id+"F0.wireOp",EDGE,"E0.left");Q14=makeQuery(id+"F0.imprint","IMPRINT",FACE,{"disambiguationData":[TD([[makeQuery(id+"F0.imprint","IMPRINT",EDGE,{"derivedFrom":subQ9}),1.0]])]});}
            var Q15;
            {var subQ0=sQuery(id+"F0.wireOp",EDGE,"gPkFda2c-Dm8t-b8RN-PjmV-kEG28G5E5dCk");var subQ1=sQuery(id+"F0.wireOp",EDGE,"E0.bottom");var subQ2=makeQuery(id+"F0.imprint","INTERSECT",VERTEX,{"disambiguationData":[OD(0.0)],"derivedFrom":[subQ1,subQ0]});Q15=makeQuery(id+"F0.imprint","IMPRINT",FACE,{"disambiguationData":[TD([[makeQuery(id+"F0.imprint","IMPRINT",EDGE,{"disambiguationData":[TD([[subQ2,-1.0]])],"derivedFrom":subQ1}),-1.0]])]});}
            var Q16;
            Q16=makeQuery(id+"F0.imprint","IMPRINT",FACE,{"disambiguationData":[TD([[makeQuery(id+"F0.imprint","IMPRINT",EDGE,{"derivedFrom":sQuery(id+"F0.wireOp",EDGE,"E30")}),1.0]])]});
            extrude(context, id + "F3", {"entities" : qUnion([Q0, Q1, Q2, Q3, Q4, Q5, Q6, Q7, Q8, Q9, Q10, Q11, Q12, Q13, Q14, Q15, Q16]), "depth" : 3 * mm});
        }
    });
